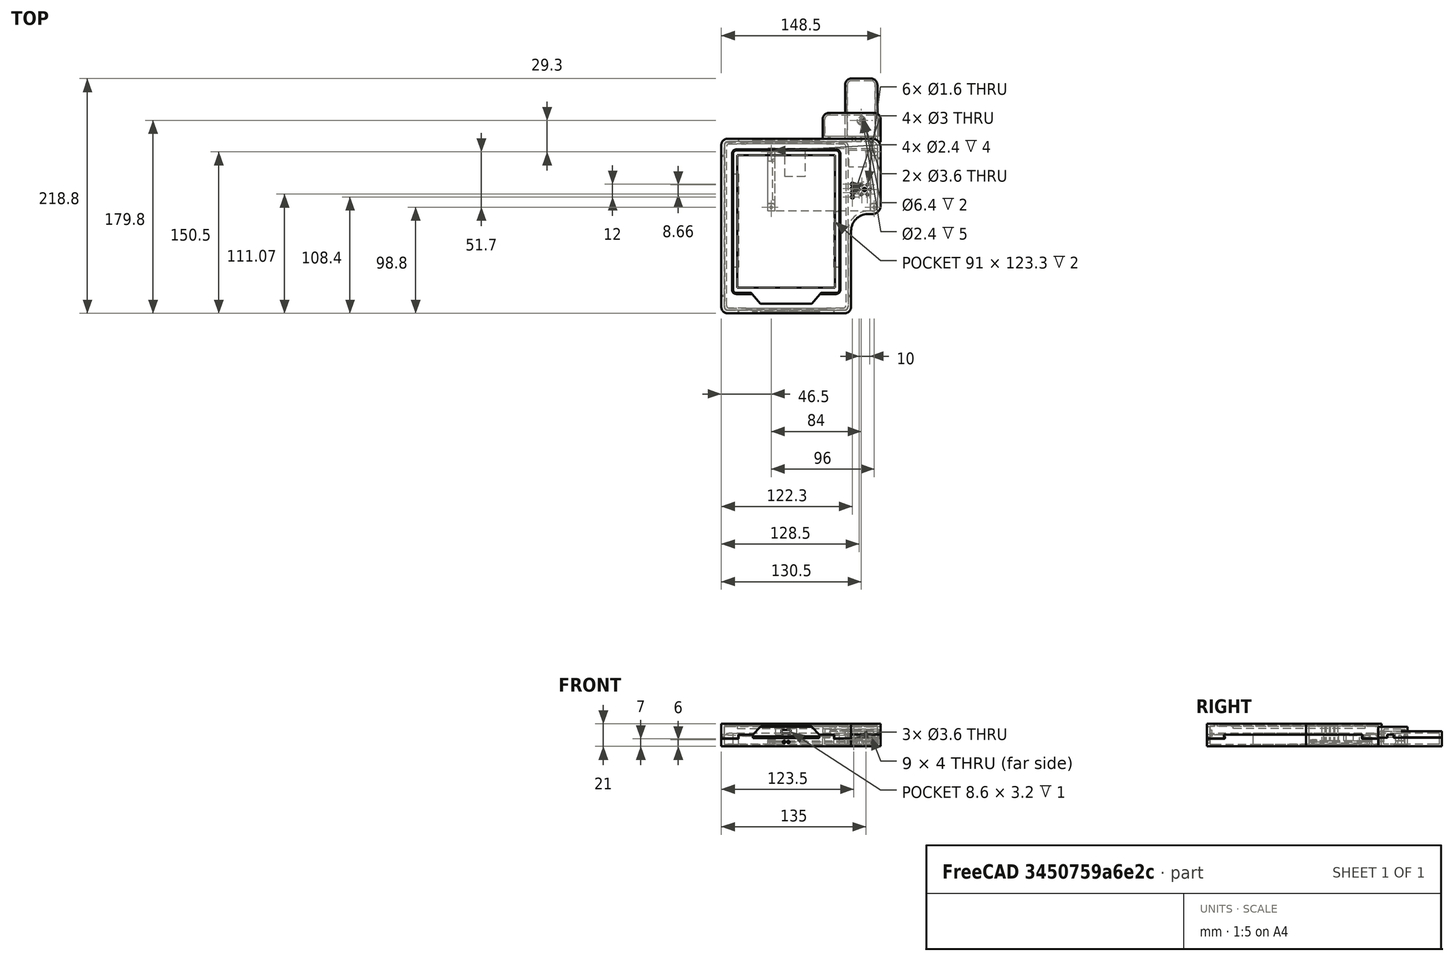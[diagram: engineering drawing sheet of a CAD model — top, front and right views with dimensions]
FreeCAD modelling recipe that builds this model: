
FCSTD DOCUMENT  (FreeCAD 0.18R16131 (Git))
Label: Kobo
License: All rights reserved
LicenseURL: http://en.wikipedia.org/wiki/All_rights_reserved
objects: Sketcher::SketchObject×69, PartDesign::Pocket×30, PartDesign::Pad×20, PartDesign::Plane×18, PartDesign::ShapeBinder×14, PartDesign::Body×10, PartDesign::Fillet×5, PartDesign::SubtractiveLoft×4, PartDesign::AdditiveLoft×4, PartDesign::Chamfer×4, Mesh::Feature×2
note: 236 computed .brp shape members not serialized (recipe doc carries the construction recipe); baked Part::Feature solids carry a one-line shape summary decoded from their .brp

FEATURE [Sketcher::SketchObject] Sketch  label="Kobo-Outline"
  MapMode = 5
  Support = -> [XY_Plane]
  sketch-geometry (4):
    g0: LineSegment StartX=-57.5 StartY=78.4 StartZ=0 EndX=57.5 EndY=78.4 EndZ=0
    g1: LineSegment StartX=57.5 StartY=78.4 StartZ=0 EndX=57.5 EndY=-78.4 EndZ=0
    g2: LineSegment StartX=57.5 StartY=-78.4 StartZ=0 EndX=-57.5 EndY=-78.4 EndZ=0
    g3: LineSegment StartX=-57.5 StartY=-78.4 StartZ=0 EndX=-57.5 EndY=78.4 EndZ=0
  constraints (12):
    c: Coincident(g0,g1)
    c: Coincident(g1,g2)
    c: Coincident(g2,g3)
    c: Coincident(g3,g0)
    c: Horizontal(g0)
    c: Horizontal(g2)
    c: Vertical(g1)
    c: Vertical(g3)
    c: Symmetric(g0,g0,g-2)
    c: Symmetric(g0,g1,g-1)
    c: DistanceY(g1,g1) = 156.8
    c: DistanceX(g2,g2) = 115
FEATURE [Sketcher::SketchObject] Sketch001  label="Vario-Outline"
  MapMode = 5
  Support = -> [XY_Plane]
  sketch-geometry (17):
    g0: LineSegment StartX=-17 StartY=72.5 StartZ=0 EndX=85 EndY=72.5 EndZ=0
    g1: LineSegment StartX=85 StartY=72.5 StartZ=0 EndX=85 EndY=14 EndZ=0
    g2: LineSegment StartX=85 StartY=14 StartZ=0 EndX=-17 EndY=14 EndZ=0
    g3: LineSegment StartX=-17 StartY=14 StartZ=0 EndX=-17 EndY=72.5 EndZ=0
    g4: LineSegment StartX=58.5 StartY=70.9 StartZ=0 EndX=74.5 EndY=70.9 EndZ=0
    g5: LineSegment StartX=74.5 StartY=70.9 StartZ=0 EndX=74.5 EndY=54.9 EndZ=0
    g6: LineSegment StartX=74.5 StartY=54.9 StartZ=0 EndX=58.5 EndY=54.9 EndZ=0
    g7: LineSegment StartX=58.5 StartY=54.9 StartZ=0 EndX=58.5 EndY=70.9 EndZ=0
    g8: Circle CenterX=61.8 CenterY=39 CenterZ=0 NormalX=0 NormalY=0 NormalZ=1 AngleXU=0 Radius=1.5
    g9: Circle CenterX=61.8 CenterY=35 CenterZ=0 NormalX=0 NormalY=0 NormalZ=1 AngleXU=0 Radius=1.5
    g10: Circle CenterX=61.8 CenterY=31 CenterZ=0 NormalX=0 NormalY=0 NormalZ=1 AngleXU=0 Radius=1.5
    g11: Circle CenterX=61.8 CenterY=27 CenterZ=0 NormalX=0 NormalY=0 NormalZ=1 AngleXU=0 Radius=1.5
    g12: Circle CenterX=73 CenterY=34 CenterZ=0 NormalX=0 NormalY=0 NormalZ=1 AngleXU=0 Radius=7
    g13: LineSegment StartX=-1.22 StartY=70 StartZ=0 EndX=17.58 EndY=70 EndZ=0
    g14: LineSegment StartX=17.58 StartY=70 StartZ=0 EndX=17.58 EndY=46 EndZ=0
    g15: LineSegment StartX=17.58 StartY=46 StartZ=0 EndX=-1.22 EndY=46 EndZ=0
    g16: LineSegment StartX=-1.22 StartY=46 StartZ=0 EndX=-1.22 EndY=70 EndZ=0
  constraints (51):
    c: Coincident(g0,g1)
    c: Coincident(g1,g2)
    c: Coincident(g2,g3)
    c: Coincident(g3,g0)
    c: Horizontal(g0)
    c: Horizontal(g2)
    c: Vertical(g1)
    c: Vertical(g3)
    c: DistanceY(g1,g1) = 58.5
    c: DistanceX(g2,g2) = 102
    c: DistanceX(g2,g-1) = 17
    c: DistanceY(g-1,g2) = 14
    c: Coincident(g4,g5)
    c: Coincident(g5,g6)
    c: Coincident(g6,g7)
    c: Coincident(g7,g4)
    c: Horizontal(g4)
    c: Horizontal(g6)
    c: Vertical(g5)
    c: Vertical(g7)
    c: Coincident(g13,g14)
    c: Coincident(g14,g15)
    c: Coincident(g15,g16)
    c: Coincident(g16,g13)
    c: Horizontal(g13)
    c: Horizontal(g15)
    c: Vertical(g14)
    c: Vertical(g16)
    c: Equal(g4,g5)
    c: DistanceX(g4,g4) = 16
    c: Vertical(g8,g9)
    c: Vertical(g9,g10)
    c: Vertical(g10,g11)
    c: Equal(g11,g10)
    c: Equal(g10,g9)
    c: Equal(g9,g8)
    c: Radius(g8) = 1.5
    c: DistanceX(g2,g6) = 75.5
    c: DistanceX(g2,g11) = 78.8
    c: DistanceX(g2,g12) = 90
    c: DistanceY(g2,g11) = 13
    c: DistanceY(g2,g10) = 17
    c: DistanceY(g2,g9) = 21
    c: DistanceY(g2,g8) = 25
    c: DistanceY(g14,g14) = 24
    c: DistanceX(g13,g13) = 18.8
    c: DistanceX(g2,g15) = 15.78
    c: DistanceY(g2,g15) = 32
    c: DistanceY(g1,g5) = 40.9
    c: Radius(g12) = 7
    c: DistanceY(g1,g12) = 20
FEATURE [PartDesign::ShapeBinder] ShapeBinder  label="ShapeBinder-Kobo"
  Support = -> [Sketch]
  TraceSupport = false
FEATURE [PartDesign::ShapeBinder] ShapeBinder001  label="ShapeBinder-Vario"
  Support = -> [Sketch001]
  TraceSupport = false
FEATURE [PartDesign::ShapeBinder] ShapeBinder002
  Support = -> [Sketch]
  TraceSupport = false
FEATURE [Sketcher::SketchObject] Sketch003
  MapMode = 5
  Placement = pos=(0,0,0) rot=(1,0,0;1.5708rad)
  Support = -> [XZ_Plane003]
  sketch-geometry (6):
    g0: LineSegment StartX=-57.4 StartY=6.4 StartZ=0 EndX=57.4 EndY=6.4 EndZ=0
    g1: LineSegment StartX=57.4 StartY=6.4 StartZ=0 EndX=57.4 EndY=-1.1 EndZ=0
    g2: LineSegment StartX=37.4 StartY=-2.6 StartZ=0 EndX=-37.4 EndY=-2.6 EndZ=0
    g3: LineSegment StartX=-57.4 StartY=-1.1 StartZ=0 EndX=-57.4 EndY=6.4 EndZ=0
    g4: LineSegment StartX=-57.4 StartY=-1.1 StartZ=0 EndX=-37.4 EndY=-2.6 EndZ=0
    g5: LineSegment StartX=37.4 StartY=-2.6 StartZ=0 EndX=57.4 EndY=-1.1 EndZ=0
  constraints (16):
    c: Coincident(g0,g1)
    c: Coincident(g3,g0)
    c: Vertical(g1)
    c: Vertical(g3)
    c: Coincident(g2,g5)
    c: Coincident(g1,g5)
    c: Coincident(g2,g4)
    c: Coincident(g3,g4)
    c: Symmetric(g0,g0,g-2)
    c: Equal(g3,g1)
    c: Symmetric(g2,g2,g-2)
    c: DistanceX(g0,g0) = 114.8
    c: DistanceY(g2,g-1) = 2.6
    c: DistanceY(g3,g3) = 7.5
    c: DistanceX(g3,g2) = 20
    c: DistanceY(g2,g0) = 9
FEATURE [PartDesign::Pad] Pad
  Length = 78.2
  Length2 = 78.2
  Placement = pos=(0,0,0) rot=(1,0,0;1.5708rad)
  Profile = -> Sketch003
  Type = 4
FEATURE [Sketcher::SketchObject] Sketch004
  ExternalGeometry = -> [ShapeBinder002]
  MapMode = 5
  Placement = pos=(0,4.2e-15,6.4) rot=(0,0,1;3.14159rad)
  Support = -> [Pad]
  sketch-geometry (4):
    g0: LineSegment StartX=-45.5 StartY=57.4 StartZ=0 EndX=45.5 EndY=57.4 EndZ=0
    g1: LineSegment StartX=45.5 StartY=57.4 StartZ=0 EndX=45.5 EndY=-65.9 EndZ=0
    g2: LineSegment StartX=45.5 StartY=-65.9 StartZ=0 EndX=-45.5 EndY=-65.9 EndZ=0
    g3: LineSegment StartX=-45.5 StartY=-65.9 StartZ=0 EndX=-45.5 EndY=57.4 EndZ=0
  constraints (11):
    c: Coincident(g0,g1)
    c: Coincident(g1,g2)
    c: Coincident(g2,g3)
    c: Coincident(g3,g0)
    c: Vertical(g1)
    c: Vertical(g3)
    c: Symmetric(g0,g0,g-2)
    c: DistanceX(g-3,g0) = 12
    c: DistanceY(g0,g-3) = 21
    c: Horizontal(g2)
    c: DistanceY(g-4,g1) = 12.5
FEATURE [PartDesign::Pocket] Pocket
  BaseFeature = -> Pad
  Length = 2
  Length2 = 100
  Placement = pos=(0,0,0) rot=(1,0,0;1.5708rad)
  Profile = -> Sketch004
  Type = 0
FEATURE [Sketcher::SketchObject] Sketch005
  ExternalGeometry = -> [ShapeBinder002]
  MapMode = 5
  Placement = pos=(0,-1.7e-15,-2.6) rot=(1,0,0;3.14159rad)
  Support = -> [Pocket]
  sketch-geometry (8):
    g0: LineSegment StartX=-53.5 StartY=76.4 StartZ=0 EndX=53.5 EndY=76.4 EndZ=0
    g1: LineSegment StartX=55.5 StartY=74.4 StartZ=0 EndX=55.5 EndY=-74.4 EndZ=0
    g2: LineSegment StartX=53.5 StartY=-76.4 StartZ=0 EndX=-53.5 EndY=-76.4 EndZ=0
    g3: LineSegment StartX=-55.5 StartY=-74.4 StartZ=0 EndX=-55.5 EndY=74.4 EndZ=0
    g4: ArcOfCircle CenterX=-53.5 CenterY=74.4 CenterZ=0 NormalX=0 NormalY=0 NormalZ=1 AngleXU=0 Radius=2 StartAngle=1.5708 EndAngle=3.14159
    g5: ArcOfCircle CenterX=53.5 CenterY=74.4 CenterZ=0 NormalX=0 NormalY=0 NormalZ=1 AngleXU=0 Radius=2 StartAngle=-9e-16 EndAngle=1.5708
    g6: ArcOfCircle CenterX=53.5 CenterY=-74.4 CenterZ=0 NormalX=0 NormalY=0 NormalZ=1 AngleXU=0 Radius=2 StartAngle=4.71239 EndAngle=6.28319
    g7: ArcOfCircle CenterX=-53.5 CenterY=-74.4 CenterZ=0 NormalX=0 NormalY=0 NormalZ=1 AngleXU=0 Radius=2 StartAngle=3.14159 EndAngle=4.71239
  constraints (20):
    c: Horizontal(g0)
    c: Horizontal(g2)
    c: Vertical(g1)
    c: Vertical(g3)
    c: Tangent(g0,g4) = 1.5708
    c: Tangent(g3,g4) = 1.5708
    c: Tangent(g0,g5) = 1.5708
    c: Tangent(g1,g5) = 1.5708
    c: Tangent(g1,g6) = 1.5708
    c: Tangent(g2,g6) = 1.5708
    c: Tangent(g2,g7) = 1.5708
    c: Tangent(g3,g7) = 1.5708
    c: Vertical(g4,g7)
    c: Vertical(g5,g6)
    c: Horizontal(g4,g5)
    c: DistanceX(g3,g4) = 2
    c: DistanceX(g-3,g4) = 4
    c: DistanceY(g4,g-3) = 4
    c: DistanceX(g6,g-4) = 4
    c: DistanceY(g-4,g6) = 4
FEATURE [PartDesign::Pocket] Pocket001
  BaseFeature = -> Pocket
  Length = 2.6
  Length2 = 100
  Placement = pos=(0,0,0) rot=(1,0,0;1.5708rad)
  Profile = -> Sketch005
  Type = 0
FEATURE [PartDesign::Fillet] Fillet
  Base = -> Pocket001 [Edge24,Edge21,Edge4,Edge3]
  BaseFeature = -> Pocket001
  Placement = pos=(0,0,0) rot=(1,0,0;1.5708rad)
  Radius = 3
FEATURE [PartDesign::ShapeBinder] ShapeBinder003
  Support = -> [Sketch001]
  TraceSupport = false
FEATURE [Sketcher::SketchObject] Sketch006
  ExternalGeometry = -> [ShapeBinder003]
  MapMode = 5
  Support = -> [XY_Plane004]
  sketch-geometry (12):
    g0: LineSegment StartX=-10.625 StartY=72.5 StartZ=0 EndX=78.625 EndY=72.5 EndZ=0
    g1: LineSegment StartX=85 StartY=65.575 StartZ=0 EndX=85 EndY=20.925 EndZ=0
    g2: LineSegment StartX=78.625 StartY=14 StartZ=0 EndX=-10.625 EndY=14 EndZ=0
    g3: LineSegment StartX=-17 StartY=20.925 StartZ=0 EndX=-17 EndY=65.575 EndZ=0
    g4: LineSegment StartX=78.625 StartY=20.925 StartZ=0 EndX=85 EndY=20.925 EndZ=0
    g5: LineSegment StartX=78.625 StartY=14 StartZ=0 EndX=78.625 EndY=20.925 EndZ=0
    g6: LineSegment StartX=85 StartY=65.575 StartZ=0 EndX=78.625 EndY=65.575 EndZ=0
    g7: LineSegment StartX=78.625 StartY=65.575 StartZ=0 EndX=78.625 EndY=72.5 EndZ=0
    g8: LineSegment StartX=-10.625 StartY=72.5 StartZ=0 EndX=-10.625 EndY=65.575 EndZ=0
    g9: LineSegment StartX=-10.625 StartY=65.575 StartZ=0 EndX=-17 EndY=65.575 EndZ=0
    g10: LineSegment StartX=-17 StartY=20.925 StartZ=0 EndX=-10.625 EndY=20.925 EndZ=0
    g11: LineSegment StartX=-10.625 StartY=20.925 StartZ=0 EndX=-10.625 EndY=14 EndZ=0
  constraints (36):
    c: Horizontal(g0)
    c: Horizontal(g2)
    c: Vertical(g1)
    c: Vertical(g3)
    c: Coincident(g5,g4)
    c: Horizontal(g4)
    c: Vertical(g5)
    c: Coincident(g6,g7)
    c: Horizontal(g6)
    c: Vertical(g7)
    c: Coincident(g8,g9)
    c: Horizontal(g9)
    c: Vertical(g8)
    c: Coincident(g10,g11)
    c: Horizontal(g10)
    c: Vertical(g11)
    c: Coincident(g0,g8)
    c: Coincident(g3,g9)
    c: Coincident(g0,g7)
    c: Coincident(g1,g6)
    c: Coincident(g1,g4)
    c: Coincident(g2,g5)
    c: Coincident(g2,g11)
    c: Coincident(g3,g10)
    c: Vertical(g8,g10)
    c: Vertical(g6,g4)
    c: Horizontal(g6,g8)
    c: Horizontal(g10,g4)
    c: Vertical(g3,g-3)
    c: Vertical(g-4,g1)
    c: Horizontal(g2,g-5)
    c: Horizontal(g-4,g0)
    c: Equal(g8,g11)
    c: Equal(g10,g4)
    c: DistanceY(g3,g3) = 44.65
    c: DistanceX(g0,g0) = 89.25
FEATURE [PartDesign::Pad] Pad001  label="PCB"
  Length = 1.2
  Length2 = 100
  Profile = -> Sketch006
  Type = 0
FEATURE [Sketcher::SketchObject] Sketch007
  ExternalGeometry = -> [ShapeBinder003]
  MapMode = 5
  Placement = pos=(0,0,1.2) rot=(0,0,1;0rad)
  Support = -> [Pad001]
  sketch-geometry (4):
    g0: LineSegment StartX=58.5 StartY=70.9 StartZ=0 EndX=74.5 EndY=70.9 EndZ=0
    g1: LineSegment StartX=74.5 StartY=70.9 StartZ=0 EndX=74.5 EndY=54.9 EndZ=0
    g2: LineSegment StartX=74.5 StartY=54.9 StartZ=0 EndX=58.5 EndY=54.9 EndZ=0
    g3: LineSegment StartX=58.5 StartY=54.9 StartZ=0 EndX=58.5 EndY=70.9 EndZ=0
  constraints (10):
    c: Coincident(g0,g1)
    c: Coincident(g1,g2)
    c: Coincident(g2,g3)
    c: Coincident(g3,g0)
    c: Horizontal(g0)
    c: Horizontal(g2)
    c: Vertical(g1)
    c: Vertical(g3)
    c: Coincident(g-4,g2)
    c: Coincident(g-3,g0)
FEATURE [PartDesign::Pad] Pad002  label="GPS"
  BaseFeature = -> Pad001
  Length = 6.5
  Length2 = 100
  Profile = -> Sketch007
  Type = 0
FEATURE [Sketcher::SketchObject] Sketch008
  ExternalGeometry = -> [ShapeBinder003]
  MapMode = 5
  Placement = pos=(0,0,1.2) rot=(0,0,1;0rad)
  Support = -> [Pad002]
  sketch-geometry (4):
    g0: Circle CenterX=61.8 CenterY=39 CenterZ=0 NormalX=0 NormalY=0 NormalZ=1 AngleXU=0 Radius=1.5
    g1: Circle CenterX=61.8 CenterY=35 CenterZ=0 NormalX=0 NormalY=0 NormalZ=1 AngleXU=0 Radius=1.5
    g2: Circle CenterX=61.8 CenterY=31 CenterZ=0 NormalX=0 NormalY=0 NormalZ=1 AngleXU=0 Radius=1.5
    g3: Circle CenterX=61.8 CenterY=27 CenterZ=0 NormalX=0 NormalY=0 NormalZ=1 AngleXU=0 Radius=1.5
  constraints (8):
    c: Equal(g3,g2)
    c: Equal(g2,g1)
    c: Equal(g1,g0)
    c: Radius(g0) = 1.5
    c: Coincident(g3,g-6)
    c: Coincident(g-5,g2)
    c: Coincident(g-4,g1)
    c: Coincident(g-3,g0)
FEATURE [PartDesign::Pad] Pad003  label="LED"
  BaseFeature = -> Pad002
  Length = 15
  Length2 = 100
  Profile = -> Sketch008
  Type = 0
FEATURE [Sketcher::SketchObject] Sketch009
  ExternalGeometry = -> [ShapeBinder003]
  MapMode = 5
  Placement = pos=(0,0,1.2) rot=(0,0,1;0rad)
  Support = -> [Pad003]
  sketch-geometry (1):
    g0: Circle CenterX=73 CenterY=34 CenterZ=0 NormalX=0 NormalY=0 NormalZ=1 AngleXU=0 Radius=7
  constraints (2):
    c: Radius(g0) = 7
    c: Coincident(g0,g-3)
FEATURE [PartDesign::Pad] Pad004  label="PIEZO"
  BaseFeature = -> Pad003
  Length = 5
  Length2 = 100
  Profile = -> Sketch009
  Type = 0
FEATURE [Sketcher::SketchObject] Sketch010
  ExternalGeometry = -> [ShapeBinder003]
  MapMode = 5
  Placement = pos=(0,0,1.2) rot=(0,0,1;0rad)
  Support = -> [Pad004]
  sketch-geometry (4):
    g0: LineSegment StartX=-1.22 StartY=70 StartZ=0 EndX=17.58 EndY=70 EndZ=0
    g1: LineSegment StartX=17.58 StartY=70 StartZ=0 EndX=17.58 EndY=46 EndZ=0
    g2: LineSegment StartX=17.58 StartY=46 StartZ=0 EndX=-1.22 EndY=46 EndZ=0
    g3: LineSegment StartX=-1.22 StartY=46 StartZ=0 EndX=-1.22 EndY=70 EndZ=0
  constraints (10):
    c: Coincident(g0,g1)
    c: Coincident(g1,g2)
    c: Coincident(g2,g3)
    c: Coincident(g3,g0)
    c: Horizontal(g0)
    c: Horizontal(g2)
    c: Vertical(g1)
    c: Vertical(g3)
    c: Coincident(g0,g-3)
    c: Coincident(g-4,g2)
FEATURE [PartDesign::Pad] Pad005  label="IMU"
  BaseFeature = -> Pad004
  Length = 4.8
  Length2 = 100
  Profile = -> Sketch010
  Type = 0
FEATURE [PartDesign::Body] Body004  label="Vario"
  Group = -> [ShapeBinder003,Sketch006,Pad001,Sketch007,Pad002,Sketch008,Pad003,Sketch009,Pad004,Sketch010,Pad005]
  Origin = -> Origin004
  Placement = pos=(0,0,4) rot=(0,0,1;0rad)
  Tip = -> Pad005
FEATURE [Sketcher::SketchObject] Sketch012
  ExternalGeometry = -> [Fillet]
  MapMode = 5
  Placement = pos=(0,-78.2,3.46e-14) rot=(1,0,0;1.5708rad)
  Support = -> [Fillet]
  sketch-geometry (4):
    g0: LineSegment StartX=-4.3 StartY=3.2 StartZ=0 EndX=4.3 EndY=3.2 EndZ=0
    g1: LineSegment StartX=4.3 StartY=3.2 StartZ=0 EndX=4.3 EndY=9e-16 EndZ=0
    g2: LineSegment StartX=4.3 StartY=9e-16 StartZ=0 EndX=-4.3 EndY=9e-16 EndZ=0
    g3: LineSegment StartX=-4.3 StartY=9e-16 StartZ=0 EndX=-4.3 EndY=3.2 EndZ=0
  constraints (11):
    c: Coincident(g0,g1)
    c: Coincident(g1,g2)
    c: Coincident(g2,g3)
    c: Coincident(g3,g0)
    c: Horizontal(g0)
    c: Vertical(g1)
    c: Vertical(g3)
    c: Symmetric(g2,g1,g-2)
    c: DistanceX(g2,g2) = 8.6
    c: DistanceY(g1,g1) = 3.2
    c: DistanceY(g-3,g1) = 2.6
FEATURE [PartDesign::Pocket] Pocket003
  BaseFeature = -> Fillet
  Length = 1
  Length2 = 100
  Placement = pos=(0,0,0) rot=(1,0,0;1.5708rad)
  Profile = -> Sketch012
  Type = 0
FEATURE [Sketcher::SketchObject] Sketch013
  ExternalGeometry = -> [Pocket003]
  MapMode = 5
  Placement = pos=(0,78.2,-3.46e-14) rot=(-1,0,0;1.5708rad)
  Support = -> [Pocket003]
  sketch-geometry (4):
    g0: LineSegment StartX=-10 StartY=1 StartZ=0 EndX=10 EndY=1 EndZ=0
    g1: LineSegment StartX=10 StartY=1 StartZ=0 EndX=10 EndY=-4.6 EndZ=0
    g2: LineSegment StartX=10 StartY=-4.6 StartZ=0 EndX=-10 EndY=-4.6 EndZ=0
    g3: LineSegment StartX=-10 StartY=-4.6 StartZ=0 EndX=-10 EndY=1 EndZ=0
  constraints (11):
    c: Coincident(g0,g1)
    c: Coincident(g1,g2)
    c: Coincident(g2,g3)
    c: Coincident(g3,g0)
    c: Horizontal(g0)
    c: Vertical(g1)
    c: Vertical(g3)
    c: Symmetric(g2,g1,g-2)
    c: DistanceX(g2,g2) = 20
    c: DistanceY(g1,g1) = 5.6
    c: DistanceY(g0,g-3) = 1.6
FEATURE [PartDesign::Pocket] Pocket004
  BaseFeature = -> Pocket003
  Length = 1
  Length2 = 100
  Placement = pos=(0,0,0) rot=(1,0,0;1.5708rad)
  Profile = -> Sketch013
  Type = 0
FEATURE [PartDesign::Body] Body003  label="Kobo"
  Group = -> [ShapeBinder002,Sketch003,Pad,Sketch004,Pocket,Sketch005,Pocket001,Fillet,Sketch012,Pocket003,Sketch013,Pocket004]
  Origin = -> Origin003
  Placement = pos=(0,0,12) rot=(0,0,1;0rad)
  Tip = -> Pocket004
FEATURE [PartDesign::ShapeBinder] ShapeBinder004  label="ShapeBinder-Kobo-Cover"
  Support = -> [Sketch]
  TraceSupport = false
FEATURE [PartDesign::ShapeBinder] ShapeBinder005  label="ShapeBinder-Vario-Cover"
  Support = -> [Sketch001]
  TraceSupport = false
FEATURE [Sketcher::SketchObject] Sketch014
  ExternalGeometry = -> [ShapeBinder004,ShapeBinder005]
  MapMode = 5
  Support = -> [XY_Plane002]
  sketch-geometry (12):
    g0: LineSegment StartX=-54.5 StartY=81.4 StartZ=0 EndX=80 EndY=81.4 EndZ=0
    g1: LineSegment StartX=88 StartY=73.4 StartZ=0 EndX=88 EndY=19 EndZ=0
    g2: LineSegment StartX=54.5 StartY=-81.4 StartZ=0 EndX=-54.5 EndY=-81.4 EndZ=0
    g3: LineSegment StartX=-60.5 StartY=-75.4 StartZ=0 EndX=-60.5 EndY=75.4 EndZ=0
    g4: LineSegment StartX=76 StartY=11 StartZ=0 EndX=80 EndY=11 EndZ=0
    g5: LineSegment StartX=60.5 StartY=-75.4 StartZ=0 EndX=60.5 EndY=-4.5 EndZ=0
    g6: ArcOfCircle CenterX=-54.5 CenterY=75.4 CenterZ=0 NormalX=0 NormalY=0 NormalZ=1 AngleXU=0 Radius=6 StartAngle=1.5708 EndAngle=3.14159
    g7: ArcOfCircle CenterX=80 CenterY=73.4 CenterZ=0 NormalX=0 NormalY=0 NormalZ=1 AngleXU=0 Radius=8 StartAngle=-9e-16 EndAngle=1.5708
    g8: ArcOfCircle CenterX=80 CenterY=19 CenterZ=0 NormalX=0 NormalY=0 NormalZ=1 AngleXU=0 Radius=8 StartAngle=4.71239 EndAngle=6.28319
    g9: ArcOfCircle CenterX=76 CenterY=-4.5 CenterZ=0 NormalX=0 NormalY=0 NormalZ=1 AngleXU=0 Radius=15.5 StartAngle=1.5708 EndAngle=3.14159
    g10: ArcOfCircle CenterX=54.5 CenterY=-75.4 CenterZ=0 NormalX=0 NormalY=0 NormalZ=1 AngleXU=0 Radius=6 StartAngle=4.71239 EndAngle=6.28319
    g11: ArcOfCircle CenterX=-54.5 CenterY=-75.4 CenterZ=0 NormalX=0 NormalY=0 NormalZ=1 AngleXU=0 Radius=6 StartAngle=3.14159 EndAngle=4.71239
  constraints (30):
    c: Horizontal(g0)
    c: Horizontal(g2)
    c: Vertical(g1)
    c: Vertical(g3)
    c: Horizontal(g4)
    c: Vertical(g5)
    c: Tangent(g0,g6) = 1.5708
    c: Tangent(g3,g6) = 1.5708
    c: Tangent(g0,g7) = 1.5708
    c: Tangent(g1,g7) = 1.5708
    c: Tangent(g1,g8) = 1.5708
    c: Tangent(g4,g8) = -1.5708
    c: Tangent(g4,g9) = 1.5708
    c: Tangent(g5,g9) = 1.5708
    c: Tangent(g2,g10) = 1.5708
    c: Tangent(g5,g10) = -1.5708
    c: Tangent(g2,g11) = 1.5708
    c: Tangent(g3,g11) = 1.5708
    c: Vertical(g6,g11)
    c: Horizontal(g11,g10)
    c: DistanceX(g3,g11) = 6
    c: DistanceY(g-3,g0) = 3
    c: DistanceX(g3,g-3) = 3
    c: DistanceX(g-5,g1) = 3
    c: DistanceY(g4,g-5) = 3
    c: DistanceY(g2,g-4) = 3
    c: DistanceX(g-4,g5) = 3
    c: DistanceX(g4,g4) = 4
    c: Vertical(g8,g7)
    c: DistanceX(g7,g1) = 8
FEATURE [PartDesign::Pad] Pad007
  Length = 10
  Length2 = 100
  Profile = -> Sketch014
  Reversed = true
  Type = 0
FEATURE [Sketcher::SketchObject] Sketch015
  ExternalGeometry = -> [ShapeBinder,ShapeBinder001]
  MapMode = 5
  Support = -> [XY_Plane001]
  sketch-geometry (12):
    g0: LineSegment StartX=-54.5 StartY=81.4 StartZ=0 EndX=80 EndY=81.4 EndZ=0
    g1: LineSegment StartX=88 StartY=73.4 StartZ=0 EndX=88 EndY=19 EndZ=0
    g2: LineSegment StartX=54.5 StartY=-81.4 StartZ=0 EndX=-54.5 EndY=-81.4 EndZ=0
    g3: LineSegment StartX=-60.5 StartY=-75.4 StartZ=0 EndX=-60.5 EndY=75.4 EndZ=0
    g4: LineSegment StartX=76 StartY=11 StartZ=0 EndX=80 EndY=11 EndZ=0
    g5: LineSegment StartX=60.5 StartY=-75.4 StartZ=0 EndX=60.5 EndY=-4.5 EndZ=0
    g6: ArcOfCircle CenterX=-54.5 CenterY=75.4 CenterZ=0 NormalX=0 NormalY=0 NormalZ=1 AngleXU=0 Radius=6 StartAngle=1.5708 EndAngle=3.14159
    g7: ArcOfCircle CenterX=80 CenterY=73.4 CenterZ=0 NormalX=0 NormalY=0 NormalZ=1 AngleXU=0 Radius=8 StartAngle=0 EndAngle=1.5708
    g8: ArcOfCircle CenterX=80 CenterY=19 CenterZ=0 NormalX=0 NormalY=0 NormalZ=1 AngleXU=0 Radius=8 StartAngle=4.71239 EndAngle=6.28319
    g9: ArcOfCircle CenterX=76 CenterY=-4.5 CenterZ=0 NormalX=0 NormalY=0 NormalZ=1 AngleXU=0 Radius=15.5 StartAngle=1.5708 EndAngle=3.14159
    g10: ArcOfCircle CenterX=54.5 CenterY=-75.4 CenterZ=0 NormalX=0 NormalY=0 NormalZ=1 AngleXU=0 Radius=6 StartAngle=4.71239 EndAngle=6.28319
    g11: ArcOfCircle CenterX=-54.5 CenterY=-75.4 CenterZ=0 NormalX=0 NormalY=0 NormalZ=1 AngleXU=0 Radius=6 StartAngle=3.14159 EndAngle=4.71239
  constraints (30):
    c: Horizontal(g0)
    c: Horizontal(g2)
    c: Vertical(g1)
    c: Vertical(g3)
    c: Horizontal(g4)
    c: Vertical(g5)
    c: Tangent(g0,g6) = 1.5708
    c: Tangent(g3,g6) = 1.5708
    c: Tangent(g0,g7) = 1.5708
    c: Tangent(g1,g7) = 1.5708
    c: Tangent(g1,g8) = 1.5708
    c: Tangent(g4,g8) = -1.5708
    c: Tangent(g4,g9) = 1.5708
    c: Tangent(g5,g9) = 1.5708
    c: Tangent(g2,g10) = 1.5708
    c: Tangent(g5,g10) = -1.5708
    c: Tangent(g2,g11) = 1.5708
    c: Tangent(g3,g11) = 1.5708
    c: Vertical(g11,g6)
    c: Horizontal(g11,g10)
    c: Vertical(g8,g7)
    c: DistanceY(g2,g11) = 6
    c: DistanceX(g-4,g5) = 3
    c: DistanceX(g3,g-4) = 3
    c: DistanceY(g-3,g0) = 3
    c: DistanceY(g7,g0) = 8
    c: DistanceX(g-5,g1) = 3
    c: DistanceY(g4,g-5) = 3
    c: DistanceX(g4,g4) = 4
    c: DistanceY(g2,g-4) = 3
FEATURE [PartDesign::Pad] Pad008
  Length = 11
  Length2 = 100
  Profile = -> Sketch015
  Type = 0
FEATURE [Sketcher::SketchObject] Sketch016
  ExternalGeometry = -> [ShapeBinder,ShapeBinder001]
  MapMode = 5
  Placement = pos=(0,0,11) rot=(0,0,1;0rad)
  Support = -> [Pad008]
  sketch-geometry (12):
    g0: LineSegment StartX=-54.7 StartY=78.6 StartZ=0 EndX=80.2 EndY=78.6 EndZ=0
    g1: LineSegment StartX=85.2 StartY=73.6 StartZ=0 EndX=85.2 EndY=18.8 EndZ=0
    g2: LineSegment StartX=54.7 StartY=-78.6 StartZ=0 EndX=-54.7 EndY=-78.6 EndZ=0
    g3: LineSegment StartX=-57.7 StartY=-75.6 StartZ=0 EndX=-57.7 EndY=75.6 EndZ=0
    g4: LineSegment StartX=76.2 StartY=13.8 StartZ=0 EndX=80.2 EndY=13.8 EndZ=0
    g5: LineSegment StartX=57.7 StartY=-75.6 StartZ=0 EndX=57.7 EndY=-4.7 EndZ=0
    g6: ArcOfCircle CenterX=-54.7 CenterY=75.6 CenterZ=0 NormalX=0 NormalY=0 NormalZ=1 AngleXU=0 Radius=3 StartAngle=1.5708 EndAngle=3.14159
    g7: ArcOfCircle CenterX=80.2 CenterY=73.6 CenterZ=0 NormalX=0 NormalY=0 NormalZ=1 AngleXU=0 Radius=5 StartAngle=1.3e-15 EndAngle=1.5708
    g8: ArcOfCircle CenterX=80.2 CenterY=18.8 CenterZ=0 NormalX=0 NormalY=0 NormalZ=1 AngleXU=0 Radius=5 StartAngle=4.71239 EndAngle=6.28319
    g9: ArcOfCircle CenterX=76.2 CenterY=-4.7 CenterZ=0 NormalX=0 NormalY=0 NormalZ=1 AngleXU=0 Radius=18.5 StartAngle=1.5708 EndAngle=3.14159
    g10: ArcOfCircle CenterX=54.7 CenterY=-75.6 CenterZ=0 NormalX=0 NormalY=0 NormalZ=1 AngleXU=0 Radius=3 StartAngle=4.71239 EndAngle=6.28319
    g11: ArcOfCircle CenterX=-54.7 CenterY=-75.6 CenterZ=0 NormalX=0 NormalY=0 NormalZ=1 AngleXU=0 Radius=3 StartAngle=3.14159 EndAngle=4.71239
  constraints (30):
    c: Horizontal(g0)
    c: Horizontal(g2)
    c: Vertical(g1)
    c: Vertical(g3)
    c: Horizontal(g4)
    c: Vertical(g5)
    c: Tangent(g0,g6) = 1.5708
    c: Tangent(g3,g6) = 1.5708
    c: Tangent(g0,g7) = 1.5708
    c: Tangent(g1,g7) = 1.5708
    c: Tangent(g1,g8) = 1.5708
    c: Tangent(g4,g8) = -1.5708
    c: Tangent(g4,g9) = 1.5708
    c: Tangent(g5,g9) = 1.5708
    c: Tangent(g2,g10) = 1.5708
    c: Tangent(g5,g10) = -1.5708
    c: Tangent(g2,g11) = 1.5708
    c: Tangent(g3,g11) = 1.5708
    c: Vertical(g6,g11)
    c: Horizontal(g11,g10)
    c: Vertical(g7,g8)
    c: DistanceY(g2,g11) = 3
    c: DistanceX(g3,g-5) = 0.2
    c: DistanceY(g2,g-5) = 0.2
    c: DistanceX(g-5,g5) = 0.2
    c: DistanceY(g4,g-4) = 0.2
    c: DistanceX(g-4,g1) = 0.2
    c: DistanceY(g-3,g0) = 0.2
    c: DistanceY(g7,g0) = 5
    c: DistanceX(g4,g4) = 4
FEATURE [PartDesign::Pocket] Pocket005
  BaseFeature = -> Pad008
  Length = 9
  Length2 = 100
  Profile = -> Sketch016
  Type = 0
FEATURE [Sketcher::SketchObject] Sketch017
  ExternalGeometry = -> [ShapeBinder004,ShapeBinder005]
  MapMode = 5
  Placement = pos=(0,0,-10) rot=(1,0,0;3.14159rad)
  Support = -> [Pad007]
  sketch-geometry (12):
    g0: LineSegment StartX=-54.7 StartY=78.6 StartZ=0 EndX=54.7 EndY=78.6 EndZ=0
    g1: LineSegment StartX=85.2 StartY=-18.8 StartZ=0 EndX=85.2 EndY=-73.6 EndZ=0
    g2: LineSegment StartX=80.2 StartY=-78.6 StartZ=0 EndX=-54.7 EndY=-78.6 EndZ=0
    g3: LineSegment StartX=-57.7 StartY=-75.6 StartZ=0 EndX=-57.7 EndY=75.6 EndZ=0
    g4: LineSegment StartX=80.2 StartY=-13.8 StartZ=0 EndX=76.2 EndY=-13.8 EndZ=0
    g5: LineSegment StartX=57.7 StartY=4.7 StartZ=0 EndX=57.7 EndY=75.6 EndZ=0
    g6: ArcOfCircle CenterX=-54.7 CenterY=75.6 CenterZ=0 NormalX=0 NormalY=0 NormalZ=1 AngleXU=0 Radius=3 StartAngle=1.5708 EndAngle=3.14159
    g7: ArcOfCircle CenterX=54.7 CenterY=75.6 CenterZ=0 NormalX=0 NormalY=0 NormalZ=1 AngleXU=0 Radius=3 StartAngle=6e-16 EndAngle=1.5708
    g8: ArcOfCircle CenterX=-54.7 CenterY=-75.6 CenterZ=0 NormalX=0 NormalY=0 NormalZ=1 AngleXU=0 Radius=3 StartAngle=3.14159 EndAngle=4.71239
    g9: ArcOfCircle CenterX=80.2 CenterY=-73.6 CenterZ=0 NormalX=0 NormalY=0 NormalZ=1 AngleXU=0 Radius=5 StartAngle=4.71239 EndAngle=6.28319
    g10: ArcOfCircle CenterX=80.2 CenterY=-18.8 CenterZ=0 NormalX=0 NormalY=0 NormalZ=1 AngleXU=0 Radius=5 StartAngle=2e-16 EndAngle=1.5708
    g11: ArcOfCircle CenterX=76.2 CenterY=4.7 CenterZ=0 NormalX=0 NormalY=0 NormalZ=1 AngleXU=0 Radius=18.5 StartAngle=3.14159 EndAngle=4.71239
  constraints (30):
    c: Horizontal(g0)
    c: Horizontal(g2)
    c: Vertical(g1)
    c: Vertical(g3)
    c: Horizontal(g4)
    c: Vertical(g5)
    c: Tangent(g0,g6) = 1.5708
    c: Tangent(g3,g6) = 1.5708
    c: Tangent(g0,g7) = 1.5708
    c: Tangent(g5,g7) = -1.5708
    c: Tangent(g2,g8) = 1.5708
    c: Tangent(g3,g8) = 1.5708
    c: Tangent(g1,g9) = 1.5708
    c: Tangent(g2,g9) = 1.5708
    c: Tangent(g1,g10) = 1.5708
    c: Tangent(g4,g10) = -1.5708
    c: Tangent(g4,g11) = 1.5708
    c: Tangent(g5,g11) = 1.5708
    c: Vertical(g9,g10)
    c: Vertical(g6,g8)
    c: Horizontal(g6,g7)
    c: DistanceY(g2,g8) = 3
    c: DistanceY(g2,g-4) = 0.2
    c: DistanceX(g3,g-4) = 0.2
    c: DistanceY(g-3,g0) = 0.2
    c: DistanceX(g-3,g5) = 0.2
    c: DistanceX(g-5,g1) = 0.2
    c: DistanceY(g2,g9) = 5
    c: DistanceX(g4,g4) = 4
    c: DistanceY(g-5,g4) = 0.2
FEATURE [PartDesign::Pocket] Pocket006
  BaseFeature = -> Pad007
  Length = 8
  Length2 = 100
  Profile = -> Sketch017
  Type = 0
FEATURE [Sketcher::SketchObject] Sketch018
  ExternalGeometry = -> [ShapeBinder004]
  MapMode = 5
  Support = -> [Pocket006]
  sketch-geometry (12):
    g0: LineSegment StartX=-46.5 StartY=70.4 StartZ=0 EndX=46.5 EndY=70.4 EndZ=0
    g1: LineSegment StartX=49.5 StartY=67.4 StartZ=0 EndX=49.5 EndY=-59.4 EndZ=0
    g2: LineSegment StartX=46.5 StartY=-62.4 StartZ=0 EndX=32.5 EndY=-62.4 EndZ=0
    g3: LineSegment StartX=-49.5 StartY=-59.4 StartZ=0 EndX=-49.5 EndY=67.4 EndZ=0
    g4: ArcOfCircle CenterX=-46.5 CenterY=67.4 CenterZ=0 NormalX=0 NormalY=0 NormalZ=1 AngleXU=0 Radius=3 StartAngle=1.5708 EndAngle=3.14159
    g5: ArcOfCircle CenterX=46.5 CenterY=67.4 CenterZ=0 NormalX=0 NormalY=0 NormalZ=1 AngleXU=0 Radius=3 StartAngle=1.9e-15 EndAngle=1.5708
    g6: ArcOfCircle CenterX=46.5 CenterY=-59.4 CenterZ=0 NormalX=0 NormalY=0 NormalZ=1 AngleXU=0 Radius=3 StartAngle=4.71239 EndAngle=6.28319
    g7: ArcOfCircle CenterX=-46.5 CenterY=-59.4 CenterZ=0 NormalX=0 NormalY=0 NormalZ=1 AngleXU=0 Radius=3 StartAngle=3.14159 EndAngle=4.71239
    g8: LineSegment StartX=32.5 StartY=-62.4 StartZ=0 EndX=24 EndY=-72.4 EndZ=0
    g9: LineSegment StartX=24 StartY=-72.4 StartZ=0 EndX=-24 EndY=-72.4 EndZ=0
    g10: LineSegment StartX=-24 StartY=-72.4 StartZ=0 EndX=-32.5 EndY=-62.4 EndZ=0
    g11: LineSegment StartX=-32.5 StartY=-62.4 StartZ=0 EndX=-46.5 EndY=-62.4 EndZ=0
  constraints (31):
    c: Horizontal(g0)
    c: Horizontal(g2)
    c: Vertical(g1)
    c: Vertical(g3)
    c: Tangent(g0,g4) = 1.5708
    c: Tangent(g3,g4) = 1.5708
    c: Tangent(g0,g5) = 1.5708
    c: Tangent(g1,g5) = 1.5708
    c: Tangent(g1,g6) = 1.5708
    c: Tangent(g2,g6) = 1.5708
    c: Coincident(g11,g7) = 1.5708
    c: Tangent(g3,g7) = 1.5708
    c: Vertical(g4,g7)
    c: Vertical(g5,g6)
    c: Horizontal(g4,g5)
    c: DistanceY(g4,g0) = 3
    c: Coincident(g8,g9)
    c: Coincident(g9,g10)
    c: Coincident(g2,g8)
    c: Tangent(g2,g11)
    c: Coincident(g10,g11)
    c: DistanceX(g-4,g3) = 8
    c: DistanceY(g0,g-3) = 8
    c: DistanceY(g-4,g8) = 6
    c: DistanceY(g-4,g2) = 16
    c: Symmetric(g9,g8,g-2)
    c: Equal(g11,g2)
    c: DistanceX(g9,g9) = 48
    c: DistanceX(g11,g11) = 14
    c: DistanceX(g1,g-4) = 8
    c: Vertical(g7,g7)
FEATURE [PartDesign::Pocket] Pocket007
  BaseFeature = -> Pocket006
  Length = 2
  Length2 = 100
  Profile = -> Sketch018
  Type = 0
FEATURE [Sketcher::SketchObject] Sketch019
  ExternalGeometry = -> [ShapeBinder001]
  MapMode = 5
  Placement = pos=(0,0,2) rot=(0,0,1;0rad)
  Support = -> [Pocket005]
  sketch-geometry (8):
    g0: LineSegment StartX=-17 StartY=72.5 StartZ=0 EndX=-10.75 EndY=72.5 EndZ=0
    g1: LineSegment StartX=-10.75 StartY=72.5 StartZ=0 EndX=-10.75 EndY=14 EndZ=0
    g2: LineSegment StartX=-10.75 StartY=14 StartZ=0 EndX=-17 EndY=14 EndZ=0
    g3: LineSegment StartX=-17 StartY=14 StartZ=0 EndX=-17 EndY=72.5 EndZ=0
    g4: LineSegment StartX=78.75 StartY=72.5 StartZ=0 EndX=85 EndY=72.5 EndZ=0
    g5: LineSegment StartX=85 StartY=72.5 StartZ=0 EndX=85 EndY=14 EndZ=0
    g6: LineSegment StartX=85 StartY=14 StartZ=0 EndX=78.75 EndY=14 EndZ=0
    g7: LineSegment StartX=78.75 StartY=14 StartZ=0 EndX=78.75 EndY=72.5 EndZ=0
  constraints (20):
    c: Coincident(g0,g1)
    c: Coincident(g1,g2)
    c: Coincident(g2,g3)
    c: Coincident(g3,g0)
    c: Horizontal(g0)
    c: Horizontal(g2)
    c: Vertical(g1)
    c: Coincident(g4,g5)
    c: Coincident(g5,g6)
    c: Coincident(g6,g7)
    c: Coincident(g7,g4)
    c: Horizontal(g4)
    c: Horizontal(g6)
    c: Vertical(g7)
    c: Coincident(g2,g-4)
    c: Coincident(g0,g-3)
    c: Coincident(g4,g-3)
    c: Coincident(g5,g-4)
    c: Equal(g0,g4)
    c: DistanceX(g0,g4) = 89.5
FEATURE [PartDesign::Pad] Pad009
  BaseFeature = -> Pocket005
  Length = 4
  Length2 = 100
  Profile = -> Sketch019
  Type = 0
FEATURE [Sketcher::SketchObject] Sketch020
  ExternalGeometry = -> [ShapeBinder001]
  MapMode = 5
  Placement = pos=(0,0,6) rot=(0,0,1;0rad)
  Support = -> [Pad009]
  sketch-geometry (8):
    g0: LineSegment StartX=-17 StartY=65.7 StartZ=0 EndX=-10.75 EndY=65.7 EndZ=0
    g1: LineSegment StartX=-10.75 StartY=65.7 StartZ=0 EndX=-10.75 EndY=20.8 EndZ=0
    g2: LineSegment StartX=-10.75 StartY=20.8 StartZ=0 EndX=-17 EndY=20.8 EndZ=0
    g3: LineSegment StartX=-17 StartY=20.8 StartZ=0 EndX=-17 EndY=65.7 EndZ=0
    g4: LineSegment StartX=78.75 StartY=65.7 StartZ=0 EndX=85 EndY=65.7 EndZ=0
    g5: LineSegment StartX=85 StartY=65.7 StartZ=0 EndX=85 EndY=20.8 EndZ=0
    g6: LineSegment StartX=85 StartY=20.8 StartZ=0 EndX=78.75 EndY=20.8 EndZ=0
    g7: LineSegment StartX=78.75 StartY=20.8 StartZ=0 EndX=78.75 EndY=65.7 EndZ=0
  constraints (24):
    c: Coincident(g0,g1)
    c: Coincident(g1,g2)
    c: Coincident(g2,g3)
    c: Coincident(g3,g0)
    c: Horizontal(g0)
    c: Horizontal(g2)
    c: Vertical(g1)
    c: Vertical(g3)
    c: Coincident(g4,g5)
    c: Coincident(g5,g6)
    c: Coincident(g6,g7)
    c: Coincident(g7,g4)
    c: Horizontal(g4)
    c: Horizontal(g6)
    c: Vertical(g5)
    c: Vertical(g7)
    c: PointOnObject(g2,g-5)
    c: PointOnObject(g5,g-6)
    c: Horizontal(g0,g4)
    c: Horizontal(g1,g6)
    c: Equal(g0,g4)
    c: DistanceY(g0,g-5) = 6.8
    c: DistanceY(g-5,g2) = 6.8
    c: DistanceX(g0,g4) = 89.5
FEATURE [PartDesign::Pocket] Pocket008
  BaseFeature = -> Pad009
  Length = 2
  Length2 = 100
  Profile = -> Sketch020
  Type = 0
FEATURE [Sketcher::SketchObject] Sketch021
  ExternalGeometry = -> [ShapeBinder001,ShapeBinder]
  MapMode = 5
  Placement = pos=(0,0,2) rot=(0,0,1;0rad)
  Support = -> [Pocket008]
  sketch-geometry (8):
    g0: LineSegment StartX=-49.5 StartY=48.4 StartZ=0 EndX=-44.5 EndY=48.4 EndZ=0
    g1: LineSegment StartX=-44.5 StartY=48.4 StartZ=0 EndX=-44.5 EndY=-38.4 EndZ=0
    g2: LineSegment StartX=-44.5 StartY=-38.4 StartZ=0 EndX=-49.5 EndY=-38.4 EndZ=0
    g3: LineSegment StartX=-49.5 StartY=-38.4 StartZ=0 EndX=-49.5 EndY=48.4 EndZ=0
    g4: LineSegment StartX=44.5 StartY=13.6 StartZ=0 EndX=49.5 EndY=13.6 EndZ=0
    g5: LineSegment StartX=49.5 StartY=13.6 StartZ=0 EndX=49.5 EndY=-38.4 EndZ=0
    g6: LineSegment StartX=49.5 StartY=-38.4 StartZ=0 EndX=44.5 EndY=-38.4 EndZ=0
    g7: LineSegment StartX=44.5 StartY=-38.4 StartZ=0 EndX=44.5 EndY=13.6 EndZ=0
  constraints (24):
    c: Coincident(g0,g1)
    c: Coincident(g1,g2)
    c: Coincident(g2,g3)
    c: Coincident(g3,g0)
    c: Horizontal(g0)
    c: Horizontal(g2)
    c: Vertical(g1)
    c: Vertical(g3)
    c: Coincident(g4,g5)
    c: Coincident(g5,g6)
    c: Coincident(g6,g7)
    c: Coincident(g7,g4)
    c: Horizontal(g4)
    c: Horizontal(g6)
    c: Vertical(g5)
    c: Vertical(g7)
    c: DistanceX(g0,g0) = 5
    c: DistanceX(g6,g6) = 5
    c: DistanceX(g5,g-4) = 8
    c: DistanceX(g-4,g2) = 8
    c: DistanceY(g-4,g2) = 40
    c: DistanceY(g0,g-5) = 30
    c: DistanceY(g4,g-3) = 0.4
    c: Horizontal(g6,g1)
FEATURE [PartDesign::Pad] Pad010
  BaseFeature = -> Pocket008
  Length = 10
  Length2 = 100
  Profile = -> Sketch021
  Type = 0
FEATURE [Sketcher::SketchObject] Sketch022
  ExternalGeometry = -> [ShapeBinder005]
  MapMode = 5
  Support = -> [Pocket007]
  sketch-geometry (18):
    g0: Circle CenterX=61.8 CenterY=39 CenterZ=0 NormalX=0 NormalY=0 NormalZ=1 AngleXU=0 Radius=1.5
    g1: Circle CenterX=61.8 CenterY=35 CenterZ=0 NormalX=0 NormalY=0 NormalZ=1 AngleXU=0 Radius=1.5
    g2: Circle CenterX=61.8 CenterY=31 CenterZ=0 NormalX=0 NormalY=0 NormalZ=1 AngleXU=0 Radius=1.5
    g3: Circle CenterX=61.8 CenterY=27 CenterZ=0 NormalX=0 NormalY=0 NormalZ=1 AngleXU=0 Radius=1.5
    g4: Circle CenterX=73 CenterY=34 CenterZ=0 NormalX=0 NormalY=0 NormalZ=1 AngleXU=0 Radius=1.6
    g5: Circle CenterX=70.5 CenterY=38.3301 CenterZ=0 NormalX=0 NormalY=0 NormalZ=1 AngleXU=0 Radius=0.8
    g6: Circle CenterX=75.5 CenterY=38.3301 CenterZ=0 NormalX=0 NormalY=0 NormalZ=1 AngleXU=0 Radius=0.8
    g7: Circle CenterX=78 CenterY=34 CenterZ=0 NormalX=0 NormalY=0 NormalZ=1 AngleXU=0 Radius=0.8
    g8: Circle CenterX=75.5 CenterY=29.6699 CenterZ=0 NormalX=0 NormalY=0 NormalZ=1 AngleXU=0 Radius=0.8
    g9: Circle CenterX=70.5 CenterY=29.6699 CenterZ=0 NormalX=0 NormalY=0 NormalZ=1 AngleXU=0 Radius=0.8
    g10: Circle CenterX=68 CenterY=34 CenterZ=0 NormalX=0 NormalY=0 NormalZ=1 AngleXU=0 Radius=0.8
    g11: LineSegment [constr] StartX=75.5 StartY=29.6699 StartZ=0 EndX=78 EndY=34 EndZ=0
    g12: LineSegment [constr] StartX=78 StartY=34 StartZ=0 EndX=75.5 EndY=38.3301 EndZ=0
    g13: LineSegment [constr] StartX=75.5 StartY=38.3301 StartZ=0 EndX=70.5 EndY=38.3301 EndZ=0
    g14: LineSegment [constr] StartX=70.5 StartY=38.3301 StartZ=0 EndX=68 EndY=34 EndZ=0
    g15: LineSegment [constr] StartX=68 StartY=34 StartZ=0 EndX=70.5 EndY=29.6699 EndZ=0
    g16: LineSegment [constr] StartX=70.5 StartY=29.6699 StartZ=0 EndX=75.5 EndY=29.6699 EndZ=0
    g17: Circle [constr] CenterX=73 CenterY=34 CenterZ=0 NormalX=0 NormalY=0 NormalZ=1 AngleXU=0 Radius=5
  constraints (38):
    c: Coincident(g0,g-3)
    c: Coincident(g1,g-4)
    c: Coincident(g2,g-5)
    c: Coincident(g3,g-6)
    c: Coincident(g4,g-7)
    c: Equal(g0,g1)
    c: Equal(g1,g2)
    c: Equal(g2,g3)
    c: Radius(g0) = 1.5
    c: Radius(g4) = 1.6
    c: Coincident(g11,g12)
    c: Coincident(g12,g13)
    c: Coincident(g13,g14)
    c: Coincident(g14,g15)
    c: Coincident(g15,g16)
    c: Coincident(g16,g11)
    c: Equal(g11, g12-g16) x5
    c: PointOnObject(g11,g17)
    c: PointOnObject(g12,g17)
    c: PointOnObject(g13,g17)
    c: PointOnObject(g14,g17)
    c: PointOnObject(g15,g17)
    c: PointOnObject(g16,g17)
    c: Coincident(g4,g17)
    c: Coincident(g5,g13)
    c: Coincident(g6,g12)
    c: Coincident(g7,g11)
    c: Coincident(g8,g11)
    c: Coincident(g9,g15)
    c: Coincident(g10,g14)
    c: Horizontal(g4,g7)
    c: DistanceX(g4,g7) = 5
    c: Equal(g9,g10)
    c: Equal(g10,g5)
    c: Equal(g5,g6)
    c: Equal(g6,g7)
    c: Equal(g7,g8)
    c: Radius(g6) = 0.8
FEATURE [PartDesign::Pocket] Pocket009
  BaseFeature = -> Pocket007
  Length = 2
  Length2 = 100
  Profile = -> Sketch022
  Type = 0
FEATURE [Sketcher::SketchObject] Sketch023
  MapMode = 5
  Placement = pos=(0,81.4,0) rot=(0,0.707107,0.707107;3.14159rad)
  Support = -> [Pocket009]
  sketch-geometry (4):
    g0: LineSegment StartX=-24 StartY=-3 StartZ=0 EndX=24 EndY=-3 EndZ=0
    g1: LineSegment StartX=24 StartY=-3 StartZ=0 EndX=31 EndY=-10 EndZ=0
    g2: LineSegment StartX=31 StartY=-10 StartZ=0 EndX=-31 EndY=-10 EndZ=0
    g3: LineSegment StartX=-31 StartY=-10 StartZ=0 EndX=-24 EndY=-3 EndZ=0
  constraints (10):
    c: Coincident(g0,g1)
    c: Coincident(g1,g2)
    c: Coincident(g2,g3)
    c: Coincident(g3,g0)
    c: Symmetric(g0,g0,g-2)
    c: Symmetric(g1,g2,g-2)
    c: DistanceY(g0,g-1) = 3
    c: DistanceX(g0,g0) = 48
    c: DistanceX(g2,g2) = 62
    c: DistanceY(g1,g0) = 7
FEATURE [PartDesign::Pocket] Pocket010
  BaseFeature = -> Pocket009
  Length = 5
  Length2 = 100
  Profile = -> Sketch023
  Type = 1
FEATURE [Sketcher::SketchObject] Sketch024
  MapMode = 5
  Placement = pos=(0,-81.4,0) rot=(1,0,0;1.5708rad)
  Support = -> [Pad010]
  sketch-geometry (4):
    g0: LineSegment StartX=-31 StartY=11 StartZ=0 EndX=31 EndY=11 EndZ=0
    g1: LineSegment StartX=31 StartY=11 StartZ=0 EndX=31 EndY=9 EndZ=0
    g2: LineSegment StartX=31 StartY=9 StartZ=0 EndX=-31 EndY=9 EndZ=0
    g3: LineSegment StartX=-31 StartY=9 StartZ=0 EndX=-31 EndY=11 EndZ=0
  constraints (11):
    c: Coincident(g0,g1)
    c: Coincident(g1,g2)
    c: Coincident(g2,g3)
    c: Coincident(g3,g0)
    c: Horizontal(g2)
    c: Vertical(g1)
    c: Vertical(g3)
    c: DistanceX(g0,g0) = 62
    c: Symmetric(g0,g0,g-2)
    c: DistanceY(g3,g3) = 2
    c: DistanceY(g-1,g2) = 9
FEATURE [PartDesign::Pocket] Pocket011
  BaseFeature = -> Pad010
  Length = 5
  Length2 = 100
  Profile = -> Sketch024
  Type = 1
FEATURE [Sketcher::SketchObject] Sketch025
  ExternalGeometry = -> [ShapeBinder,ShapeBinder001]
  MapMode = 5
  Placement = pos=(0,0,11) rot=(0,0,1;0rad)
  Support = -> [Pocket011]
  sketch-geometry (32):
    g0: LineSegment StartX=-54.5 StartY=81.4 StartZ=0 EndX=-44.5 EndY=81.4 EndZ=0
    g1: LineSegment StartX=-44.5 StartY=81.4 StartZ=0 EndX=-44.5 EndY=78.6 EndZ=0
    g2: LineSegment StartX=-57.7 StartY=65.4 StartZ=0 EndX=-60.5 EndY=65.4 EndZ=0
    g3: LineSegment StartX=-60.5 StartY=65.4 StartZ=0 EndX=-60.5 EndY=75.4 EndZ=0
    g4: LineSegment StartX=-54.7 StartY=78.6 StartZ=0 EndX=-44.5 EndY=78.6 EndZ=0
    g5: LineSegment StartX=-57.7 StartY=65.4 StartZ=0 EndX=-57.7 EndY=75.6 EndZ=0
    g6: LineSegment StartX=70 StartY=81.4 StartZ=0 EndX=80 EndY=81.4 EndZ=0
    g7: LineSegment StartX=88 StartY=73.4 StartZ=0 EndX=88 EndY=63.4 EndZ=0
    g8: LineSegment StartX=88 StartY=63.4 StartZ=0 EndX=85.2 EndY=63.4 EndZ=0
    g9: LineSegment StartX=70 StartY=78.6 StartZ=0 EndX=70 EndY=81.4 EndZ=0
    g10: LineSegment StartX=70 StartY=78.6 StartZ=0 EndX=80 EndY=78.6 EndZ=0
    g11: LineSegment StartX=85.2 StartY=73.4 StartZ=0 EndX=85.2 EndY=63.4 EndZ=0
    g12: LineSegment StartX=-60.5 StartY=-65.4 StartZ=0 EndX=-57.7 EndY=-65.4 EndZ=0
    g13: LineSegment StartX=-44.5 StartY=-78.6 StartZ=0 EndX=-44.5 EndY=-81.4 EndZ=0
    g14: LineSegment StartX=-44.5 StartY=-81.4 StartZ=0 EndX=-54.5 EndY=-81.4 EndZ=0
    g15: LineSegment StartX=-60.5 StartY=-75.4 StartZ=0 EndX=-60.5 EndY=-65.4 EndZ=0
    g16: LineSegment StartX=-44.5 StartY=-78.6 StartZ=0 EndX=-54.7 EndY=-78.6 EndZ=0
    g17: LineSegment StartX=-57.7 StartY=-75.6 StartZ=0 EndX=-57.7 EndY=-65.4 EndZ=0
    g18: LineSegment StartX=57.7 StartY=-65.4 StartZ=0 EndX=60.5 EndY=-65.4 EndZ=0
    g19: LineSegment StartX=60.5 StartY=-65.4 StartZ=0 EndX=60.5 EndY=-75.4 EndZ=0
    g20: LineSegment StartX=54.5 StartY=-81.4 StartZ=0 EndX=44.5 EndY=-81.4 EndZ=0
    g21: LineSegment StartX=44.5 StartY=-81.4 StartZ=0 EndX=44.5 EndY=-78.6 EndZ=0
    g22: LineSegment StartX=57.7 StartY=-65.4 StartZ=0 EndX=57.7 EndY=-75.6 EndZ=0
    g23: LineSegment StartX=54.7 StartY=-78.6 StartZ=0 EndX=44.5 EndY=-78.6 EndZ=0
    g24: ArcOfCircle CenterX=-54.5 CenterY=75.4 CenterZ=0 NormalX=0 NormalY=0 NormalZ=1 AngleXU=0 Radius=6 StartAngle=1.5708 EndAngle=3.14159
    g25: ArcOfCircle CenterX=-54.7 CenterY=75.6 CenterZ=0 NormalX=0 NormalY=0 NormalZ=1 AngleXU=0 Radius=3 StartAngle=1.5708 EndAngle=3.14159
    g26: ArcOfCircle CenterX=80 CenterY=73.4 CenterZ=0 NormalX=0 NormalY=0 NormalZ=1 AngleXU=0 Radius=5.2 StartAngle=-1.092e-13 EndAngle=1.5708
    g27: ArcOfCircle CenterX=80 CenterY=73.4 CenterZ=0 NormalX=0 NormalY=0 NormalZ=1 AngleXU=0 Radius=8 StartAngle=0 EndAngle=1.5708
    g28: ArcOfCircle CenterX=54.7 CenterY=-75.6 CenterZ=0 NormalX=0 NormalY=0 NormalZ=1 AngleXU=0 Radius=3 StartAngle=4.71239 EndAngle=6.28319
    g29: ArcOfCircle CenterX=54.5 CenterY=-75.4 CenterZ=0 NormalX=0 NormalY=0 NormalZ=1 AngleXU=0 Radius=6 StartAngle=4.71239 EndAngle=6.28319
    g30: ArcOfCircle CenterX=-54.5 CenterY=-75.4 CenterZ=0 NormalX=0 NormalY=0 NormalZ=1 AngleXU=0 Radius=6 StartAngle=3.14159 EndAngle=4.71239
    g31: ArcOfCircle CenterX=-54.7 CenterY=-75.6 CenterZ=0 NormalX=0 NormalY=0 NormalZ=1 AngleXU=0 Radius=3 StartAngle=3.14159 EndAngle=4.71239
  constraints (89):
    c: Coincident(g0,g1)
    c: Coincident(g2,g3)
    c: Horizontal(g0)
    c: Horizontal(g2)
    c: Vertical(g1)
    c: Vertical(g3)
    c: Horizontal(g4)
    c: Vertical(g5)
    c: Coincident(g7,g8)
    c: Coincident(g9,g6)
    c: Horizontal(g6)
    c: Horizontal(g8)
    c: Vertical(g7)
    c: Vertical(g9)
    c: Horizontal(g10)
    c: Vertical(g11)
    c: Coincident(g13,g14)
    c: Coincident(g15,g12)
    c: Horizontal(g12)
    c: Horizontal(g14)
    c: Vertical(g13)
    c: Vertical(g15)
    c: Horizontal(g16)
    c: Vertical(g17)
    c: Coincident(g18,g19)
    c: Coincident(g20,g21)
    c: Horizontal(g18)
    c: Horizontal(g20)
    c: Vertical(g19)
    c: Vertical(g21)
    c: Horizontal(g23)
    c: Vertical(g22)
    c: Coincident(g4,g1)
    c: Coincident(g5,g2)
    c: Coincident(g9,g10)
    c: Coincident(g11,g8)
    c: Coincident(g18,g22)
    c: Coincident(g23,g21)
    c: Coincident(g12,g17)
    c: Coincident(g16,g13)
    c: Tangent(g0,g24) = 1.5708
    c: Tangent(g3,g24) = 1.5708
    c: Tangent(g4,g25) = 1.5708
    c: Tangent(g5,g25) = 1.5708
    c: Tangent(g10,g26) = 1.5708
    c: Tangent(g11,g26) = 1.5708
    c: Tangent(g6,g27) = 1.5708
    c: Tangent(g7,g27) = 1.5708
    c: Tangent(g22,g28) = 1.5708
    c: Tangent(g23,g28) = 1.5708
    c: Tangent(g19,g29) = 1.5708
    c: Tangent(g20,g29) = 1.5708
    c: Tangent(g14,g30) = 1.5708
    c: Tangent(g15,g30) = 1.5708
    c: Tangent(g16,g31) = 1.5708
    c: Tangent(g17,g31) = 1.5708
    c: Vertical(g24,g30)
    c: Horizontal(g30,g29)
    c: Horizontal(g31,g28)
    c: Vertical(g31,g25)
    c: DistanceX(g3,g24) = 6
    c: DistanceY(g25,g4) = 3
    c: DistanceX(g3,g-3) = 3
    c: DistanceY(g-3,g0) = 3
    c: DistanceX(g5,g-3) = 0.2
    c: DistanceY(g-3,g4) = 0.2
    c: Equal(g3,g0)
    c: DistanceX(g0,g0) = 10
    c: DistanceY(g14,g-5) = 3
    c: DistanceX(g15,g-5) = 3
    c: DistanceY(g16,g-5) = 0.2
    c: DistanceX(g17,g-5) = 0.2
    c: Equal(g14,g15)
    c: Equal(g0,g14)
    c: DistanceY(g20,g-5) = 3
    c: DistanceX(g-5,g19) = 3
    c: DistanceY(g23,g-5) = 0.2
    c: DistanceX(g-5,g22) = 0.2
    c: Equal(g19,g20)
    c: Equal(g20,g14)
    c: DistanceX(g6,g7) = 8
    c: DistanceX(g-4) = 85
    c: DistanceX(g-4,g7) = 3
    c: DistanceX(g-4,g11) = 0.2
    c: DistanceY(g-3,g6) = 3
    c: DistanceY(g-3,g10) = 0.2
    c: Horizontal(g11,g7)
    c: Equal(g7,g6)
    c: Equal(g7,g19)
FEATURE [PartDesign::Pocket] Pocket012
  BaseFeature = -> Pocket011
  Length = 4
  Length2 = 100
  Profile = -> Sketch025
  Type = 0
FEATURE [Sketcher::SketchObject] Sketch026
  ExternalGeometry = -> [ShapeBinder004,ShapeBinder005,Pocket010]
  MapMode = 5
  Placement = pos=(0,0,-10) rot=(1,0,0;3.14159rad)
  Support = -> [Pocket010]
  sketch-geometry (32):
    g0: LineSegment StartX=-54.5 StartY=81.4 StartZ=0 EndX=-44.7 EndY=81.4 EndZ=0
    g1: LineSegment StartX=-57.7 StartY=65.6 StartZ=0 EndX=-60.5 EndY=65.6 EndZ=0
    g2: LineSegment StartX=-60.5 StartY=65.6 StartZ=0 EndX=-60.5 EndY=75.4 EndZ=0
    g3: LineSegment StartX=-54.7 StartY=78.6 StartZ=0 EndX=-44.7 EndY=78.6 EndZ=0
    g4: LineSegment StartX=-57.7 StartY=65.6 StartZ=0 EndX=-57.7 EndY=75.6 EndZ=0
    g5: LineSegment StartX=54.5 StartY=81.4 StartZ=0 EndX=44.7 EndY=81.4 EndZ=0
    g6: LineSegment StartX=44.7 StartY=81.4 StartZ=0 EndX=44.7 EndY=78.6 EndZ=0
    g7: LineSegment StartX=57.7 StartY=65.6 StartZ=0 EndX=60.5 EndY=65.6 EndZ=0
    g8: LineSegment StartX=60.5 StartY=65.6 StartZ=0 EndX=60.5 EndY=75.4 EndZ=0
    g9: LineSegment StartX=54.7 StartY=78.6 StartZ=0 EndX=44.7 EndY=78.6 EndZ=0
    g10: LineSegment StartX=57.7 StartY=65.6 StartZ=0 EndX=57.7 EndY=75.6 EndZ=0
    g11: LineSegment StartX=-54.5 StartY=-81.4 StartZ=0 EndX=-44.7 EndY=-81.4 EndZ=0
    g12: LineSegment StartX=-44.7 StartY=-81.4 StartZ=0 EndX=-44.7 EndY=-78.6 EndZ=0
    g13: LineSegment StartX=-57.7 StartY=-65.6 StartZ=0 EndX=-60.5 EndY=-65.6 EndZ=0
    g14: LineSegment StartX=-60.5 StartY=-65.6 StartZ=0 EndX=-60.5 EndY=-75.4 EndZ=0
    g15: LineSegment StartX=-54.7 StartY=-78.6 StartZ=0 EndX=-44.7 EndY=-78.6 EndZ=0
    g16: LineSegment StartX=-57.7 StartY=-65.6 StartZ=0 EndX=-57.7 EndY=-75.6 EndZ=0
    g17: LineSegment StartX=80 StartY=-81.4 StartZ=0 EndX=70.2 EndY=-81.4 EndZ=0
    g18: LineSegment StartX=70.2 StartY=-81.4 StartZ=0 EndX=70.2 EndY=-78.6 EndZ=0
    g19: LineSegment StartX=85.2 StartY=-63.6 StartZ=0 EndX=88 EndY=-63.6 EndZ=0
    g20: LineSegment StartX=88 StartY=-63.6 StartZ=0 EndX=88 EndY=-73.4 EndZ=0
    g21: LineSegment StartX=80.2 StartY=-78.6 StartZ=0 EndX=70.2 EndY=-78.6 EndZ=0
    g22: LineSegment StartX=85.2 StartY=-63.6 StartZ=0 EndX=85.2 EndY=-73.6 EndZ=0
    g23: ArcOfCircle CenterX=-54.7 CenterY=-75.6 CenterZ=0 NormalX=0 NormalY=0 NormalZ=1 AngleXU=0 Radius=3 StartAngle=3.14159 EndAngle=4.71239
    g24: ArcOfCircle CenterX=-54.5 CenterY=-75.4 CenterZ=0 NormalX=0 NormalY=0 NormalZ=1 AngleXU=0 Radius=6 StartAngle=3.14159 EndAngle=4.71239
    g25: ArcOfCircle CenterX=80.2 CenterY=-73.6 CenterZ=0 NormalX=0 NormalY=0 NormalZ=1 AngleXU=0 Radius=5 StartAngle=4.71239 EndAngle=6.28319
    g26: ArcOfCircle CenterX=80 CenterY=-73.4 CenterZ=0 NormalX=0 NormalY=0 NormalZ=1 AngleXU=0 Radius=8 StartAngle=4.71239 EndAngle=6.28319
    g27: ArcOfCircle CenterX=54.7 CenterY=75.6 CenterZ=0 NormalX=0 NormalY=0 NormalZ=1 AngleXU=0 Radius=3 StartAngle=-9e-16 EndAngle=1.5708
    g28: ArcOfCircle CenterX=54.5 CenterY=75.4 CenterZ=0 NormalX=0 NormalY=0 NormalZ=1 AngleXU=0 Radius=6 StartAngle=1.2e-15 EndAngle=1.5708
    g29: ArcOfCircle CenterX=-54.5 CenterY=75.4 CenterZ=0 NormalX=0 NormalY=0 NormalZ=1 AngleXU=0 Radius=6 StartAngle=1.5708 EndAngle=3.14159
    g30: ArcOfCircle CenterX=-54.7 CenterY=75.6 CenterZ=0 NormalX=0 NormalY=0 NormalZ=1 AngleXU=0 Radius=3 StartAngle=1.5708 EndAngle=3.14159
    g31: LineSegment StartX=-44.7 StartY=81.4 StartZ=0 EndX=-44.7 EndY=78.6 EndZ=0
  constraints (88):
    c: Coincident(g1,g2)
    c: Horizontal(g0)
    c: Horizontal(g1)
    c: Vertical(g2)
    c: Horizontal(g3)
    c: Vertical(g4)
    c: Coincident(g5,g6)
    c: Coincident(g7,g8)
    c: Horizontal(g5)
    c: Horizontal(g7)
    c: Vertical(g6)
    c: Vertical(g8)
    c: Horizontal(g9)
    c: Vertical(g10)
    c: Coincident(g11,g12)
    c: Coincident(g13,g14)
    c: Horizontal(g11)
    c: Horizontal(g13)
    c: Vertical(g12)
    c: Vertical(g14)
    c: Horizontal(g15)
    c: Vertical(g16)
    c: Coincident(g17,g18)
    c: Coincident(g19,g20)
    c: Horizontal(g17)
    c: Horizontal(g19)
    c: Vertical(g18)
    c: Vertical(g20)
    c: Horizontal(g21)
    c: Vertical(g22)
    c: Coincident(g18,g21)
    c: Coincident(g22,g19)
    c: Coincident(g15,g12)
    c: Coincident(g13,g16)
    c: Coincident(g6,g9)
    c: Coincident(g10,g7)
    c: Coincident(g1,g4)
    c: Tangent(g15,g23) = -1.5708
    c: Tangent(g16,g23) = -1.5708
    c: Tangent(g11,g24) = -1.5708
    c: Tangent(g14,g24) = -1.5708
    c: Tangent(g21,g25) = 1.5708
    c: Tangent(g22,g25) = 1.5708
    c: Tangent(g17,g26) = 1.5708
    c: Tangent(g20,g26) = 1.5708
    c: Tangent(g9,g27) = -1.5708
    c: Tangent(g10,g27) = -1.5708
    c: Tangent(g5,g28) = -1.5708
    c: Tangent(g8,g28) = -1.5708
    c: Tangent(g0,g29) = 1.5708
    c: Tangent(g2,g29) = 1.5708
    c: Tangent(g3,g30) = 1.5708
    c: Tangent(g4,g30) = 1.5708
    c: Equal(g0,g2)
    c: Equal(g2,g5)
    c: Equal(g5,g8)
    c: Equal(g8,g20)
    c: Equal(g20,g17)
    c: Equal(g17,g11)
    c: Equal(g11,g14)
    c: DistanceX(g2,g0) = 6
    c: DistanceY(g-3,g0) = 3
    c: DistanceX(g2,g-3) = 3
    c: DistanceX(g4,g-3) = 0.2
    c: DistanceY(g-3,g3) = 0.2
    c: DistanceX(g-3,g8) = 3
    c: DistanceX(g-3,g10) = 0.2
    c: DistanceY(g-3,g5) = 3
    c: DistanceY(g-3,g9) = 0.2
    c: DistanceY(g11,g-5) = 3
    c: DistanceY(g15,g-5) = 0.2
    c: DistanceX(g16,g-5) = 0.2
    c: DistanceX(g14,g-5) = 3
    c: DistanceX(g17,g20) = 8
    c: DistanceX(g-4,g20) = 3
    c: DistanceY(g17,g-5) = 3
    c: DistanceX(g-4,g22) = 0.2
    c: DistanceY(g21,g-5) = 0.2
    c: DistanceX(g0,g0) = 9.8
    c: DistanceY(g4,g3) = 3
    c: Vertical(g23,g30)
    c: Vertical(g24,g29)
    c: Coincident(g0,g31)
    c: Coincident(g3,g31)
    c: Vertical(g31)
    c: Horizontal(g27,g30)
    c: Horizontal(g29,g28)
    c: Vertical(g25,g-6)
FEATURE [PartDesign::Pad] Pad011
  BaseFeature = -> Pocket010
  Length = 3.8
  Length2 = 100
  Profile = -> Sketch026
  Type = 0
FEATURE [Sketcher::SketchObject] Sketch027  label="HoleLB"
  ExternalGeometry = -> [Pocket012]
  MapMode = 5
  Placement = pos=(0,-65.4,0) rot=(1,0,0;1.5708rad)
  Support = -> [Pocket012]
  sketch-geometry (4):
    g0: LineSegment StartX=-60.5 StartY=9.4 StartZ=0 EndX=-57.7 EndY=9.4 EndZ=0
    g1: LineSegment StartX=-57.7 StartY=9.4 StartZ=0 EndX=-57.7 EndY=7 EndZ=0
    g2: LineSegment StartX=-57.7 StartY=7 StartZ=0 EndX=-60.5 EndY=7 EndZ=0
    g3: LineSegment StartX=-60.5 StartY=7 StartZ=0 EndX=-60.5 EndY=9.4 EndZ=0
  constraints (11):
    c: Coincident(g0,g1)
    c: Coincident(g1,g2)
    c: Coincident(g2,g3)
    c: Coincident(g3,g0)
    c: Horizontal(g0)
    c: Horizontal(g2)
    c: Vertical(g1)
    c: Vertical(g3)
    c: Coincident(g2,g-3)
    c: PointOnObject(g0,g-4)
    c: DistanceY(g3,g3) = 2.4
FEATURE [Sketcher::SketchObject] Sketch028  label="HoleRT"
  ExternalGeometry = -> [Pocket012]
  MapMode = 5
  Placement = pos=(0,63.4,0) rot=(0,0.707107,0.707107;3.14159rad)
  sketch-geometry (4):
    g0: LineSegment StartX=-88 StartY=9.4 StartZ=0 EndX=-85.2 EndY=9.4 EndZ=0
    g1: LineSegment StartX=-85.2 StartY=9.4 StartZ=0 EndX=-85.2 EndY=7 EndZ=0
    g2: LineSegment StartX=-85.2 StartY=7 StartZ=0 EndX=-88 EndY=7 EndZ=0
    g3: LineSegment StartX=-88 StartY=7 StartZ=0 EndX=-88 EndY=9.4 EndZ=0
  constraints (11):
    c: Coincident(g0,g1)
    c: Coincident(g1,g2)
    c: Coincident(g2,g3)
    c: Coincident(g3,g0)
    c: Horizontal(g0)
    c: Horizontal(g2)
    c: Vertical(g1)
    c: Vertical(g3)
    c: DistanceY(g3,g3) = 2.4
    c: Coincident(g1,g-3)
    c: PointOnObject(g0,g-4)
FEATURE [Sketcher::SketchObject] Sketch029  label="HoleLT"
  ExternalGeometry = -> [Pocket012]
  MapMode = 5
  Placement = pos=(0,65.4,0) rot=(0,0.707107,0.707107;3.14159rad)
  sketch-geometry (4):
    g0: LineSegment StartX=57.7 StartY=9.4 StartZ=0 EndX=60.5 EndY=9.4 EndZ=0
    g1: LineSegment StartX=60.5 StartY=9.4 StartZ=0 EndX=60.5 EndY=7 EndZ=0
    g2: LineSegment StartX=60.5 StartY=7 StartZ=0 EndX=57.7 EndY=7 EndZ=0
    g3: LineSegment StartX=57.7 StartY=7 StartZ=0 EndX=57.7 EndY=9.4 EndZ=0
  constraints (11):
    c: Coincident(g0,g1)
    c: Coincident(g1,g2)
    c: Coincident(g2,g3)
    c: Coincident(g3,g0)
    c: Horizontal(g0)
    c: Horizontal(g2)
    c: Vertical(g1)
    c: Vertical(g3)
    c: DistanceY(g1,g1) = 2.4
    c: Coincident(g1,g-4)
    c: PointOnObject(g0,g-3)
FEATURE [Sketcher::SketchObject] Sketch030  label="HoleRB"
  ExternalGeometry = -> [Pocket012]
  MapMode = 5
  Placement = pos=(0,-65.4,0) rot=(1,0,0;1.5708rad)
  Support = -> [Pocket012]
  sketch-geometry (4):
    g0: LineSegment StartX=57.7 StartY=9.4 StartZ=0 EndX=60.5 EndY=9.4 EndZ=0
    g1: LineSegment StartX=60.5 StartY=9.4 StartZ=0 EndX=60.5 EndY=7 EndZ=0
    g2: LineSegment StartX=60.5 StartY=7 StartZ=0 EndX=57.7 EndY=7 EndZ=0
    g3: LineSegment StartX=57.7 StartY=7 StartZ=0 EndX=57.7 EndY=9.4 EndZ=0
  constraints (11):
    c: Coincident(g0,g1)
    c: Coincident(g1,g2)
    c: Coincident(g2,g3)
    c: Coincident(g3,g0)
    c: Horizontal(g0)
    c: Horizontal(g2)
    c: Vertical(g1)
    c: Vertical(g3)
    c: Coincident(g1,g-4)
    c: PointOnObject(g0,g-3)
    c: DistanceY(g1,g1) = 2.4
FEATURE [PartDesign::Plane] DatumPlane  label="DatumPlane-HoleBottom"
  AttachmentOffset = pos=(0,0,-0.6) rot=(0,0,1;0rad)
  Length = 159.932
  MapMode = 5
  Placement = pos=(0,-64.8,-1e-16) rot=(1,0,0;1.5708rad)
  ResizeMode = 0
  Support = -> [Pocket012]
  Width = 33.4315
FEATURE [PartDesign::Plane] DatumPlane001  label="DatumPlane-HoleRT"
  AttachmentOffset = pos=(0,0,-0.6) rot=(0,0,1;0rad)
  Length = 159.932
  MapMode = 5
  Placement = pos=(0,62.8,1e-16) rot=(0,0.707107,0.707107;3.14159rad)
  ResizeMode = 0
  Support = -> [Pocket012]
  Width = 33.4315
FEATURE [PartDesign::Plane] DatumPlane002  label="DatumPlane-HoleLT"
  AttachmentOffset = pos=(0,0,-0.6) rot=(0,0,1;0rad)
  Length = 159.932
  MapMode = 5
  Placement = pos=(0,64.8,1e-16) rot=(0,0.707107,0.707107;3.14159rad)
  ResizeMode = 0
  Support = -> [Pocket012]
  Width = 33.4315
FEATURE [Sketcher::SketchObject] Sketch032  label="HoleLB2"
  ExternalGeometry = -> [Pocket012]
  MapMode = 5
  Placement = pos=(0,-64.8,-1e-16) rot=(1,0,0;1.5708rad)
  Support = -> [DatumPlane]
  sketch-geometry (4):
    g0: LineSegment StartX=-60.5 StartY=9 StartZ=0 EndX=-57.7 EndY=9 EndZ=0
    g1: LineSegment StartX=-57.7 StartY=9 StartZ=0 EndX=-57.7 EndY=7.4 EndZ=0
    g2: LineSegment StartX=-57.7 StartY=7.4 StartZ=0 EndX=-60.5 EndY=7.4 EndZ=0
    g3: LineSegment StartX=-60.5 StartY=7.4 StartZ=0 EndX=-60.5 EndY=9 EndZ=0
  constraints (12):
    c: Coincident(g0,g1)
    c: Coincident(g1,g2)
    c: Coincident(g2,g3)
    c: Coincident(g3,g0)
    c: Horizontal(g0)
    c: Horizontal(g2)
    c: Vertical(g1)
    c: Vertical(g3)
    c: DistanceY(g3,g3) = 1.6
    c: PointOnObject(g1,g-3)
    c: PointOnObject(g2,g-4)
    c: DistanceY(g-3,g1) = 0.4
FEATURE [Sketcher::SketchObject] Sketch033  label="HoleRB2"
  ExternalGeometry = -> [Sketch030]
  MapMode = 5
  Placement = pos=(0,-64.8,-1e-16) rot=(1,0,0;1.5708rad)
  Support = -> [DatumPlane]
  sketch-geometry (4):
    g0: LineSegment StartX=57.7 StartY=9 StartZ=0 EndX=60.5 EndY=9 EndZ=0
    g1: LineSegment StartX=60.5 StartY=9 StartZ=0 EndX=60.5 EndY=7.4 EndZ=0
    g2: LineSegment StartX=60.5 StartY=7.4 StartZ=0 EndX=57.7 EndY=7.4 EndZ=0
    g3: LineSegment StartX=57.7 StartY=7.4 StartZ=0 EndX=57.7 EndY=9 EndZ=0
  constraints (12):
    c: Coincident(g0,g1)
    c: Coincident(g1,g2)
    c: Coincident(g2,g3)
    c: Coincident(g3,g0)
    c: Horizontal(g0)
    c: Horizontal(g2)
    c: Vertical(g1)
    c: Vertical(g3)
    c: PointOnObject(g1,g-3)
    c: PointOnObject(g2,g-4)
    c: DistanceY(g-3,g1) = 0.4
    c: DistanceY(g1,g1) = 1.6
FEATURE [PartDesign::SubtractiveLoft] SubtractiveLoft  label="SubtractiveLB"
  BaseFeature = -> Pocket012
  Closed = false
  Profile = -> Sketch027
  Ruled = false
  Sections = -> [Sketch032]
FEATURE [PartDesign::SubtractiveLoft] SubtractiveLoft001  label="SubtractiveRB"
  BaseFeature = -> SubtractiveLoft
  Closed = false
  Profile = -> Sketch030
  Ruled = false
  Sections = -> [Sketch033]
FEATURE [Sketcher::SketchObject] Sketch034  label="HolleLT2"
  ExternalGeometry = -> [SubtractiveLoft001]
  MapMode = 5
  Placement = pos=(0,64.8,1e-16) rot=(0,0.707107,0.707107;3.14159rad)
  Support = -> [DatumPlane002]
  sketch-geometry (4):
    g0: LineSegment StartX=57.7 StartY=9 StartZ=0 EndX=60.5 EndY=9 EndZ=0
    g1: LineSegment StartX=60.5 StartY=9 StartZ=0 EndX=60.5 EndY=7.4 EndZ=0
    g2: LineSegment StartX=60.5 StartY=7.4 StartZ=0 EndX=57.7 EndY=7.4 EndZ=0
    g3: LineSegment StartX=57.7 StartY=7.4 StartZ=0 EndX=57.7 EndY=9 EndZ=0
  constraints (12):
    c: Coincident(g0,g1)
    c: Coincident(g1,g2)
    c: Coincident(g2,g3)
    c: Coincident(g3,g0)
    c: Horizontal(g0)
    c: Horizontal(g2)
    c: Vertical(g1)
    c: Vertical(g3)
    c: PointOnObject(g1,g-3)
    c: PointOnObject(g2,g-4)
    c: DistanceY(g1,g1) = 1.6
    c: DistanceY(g-3,g1) = 0.4
FEATURE [PartDesign::SubtractiveLoft] SubtractiveLoft002  label="SubtractiveLT"
  BaseFeature = -> SubtractiveLoft001
  Closed = false
  Profile = -> Sketch029
  Ruled = false
  Sections = -> [Sketch034]
FEATURE [PartDesign::Plane] DatumPlane003  label="DatumPlane-CoverB1"
  Length = 160.39
  MapMode = 5
  Placement = pos=(0,-65.6,0) rot=(0,0.707107,0.707107;3.14159rad)
  ResizeMode = 0
  Support = -> [Pad011]
  Width = 35.69
FEATURE [PartDesign::Plane] DatumPlane004  label="DatumPlane-CoverB2"
  AttachmentOffset = pos=(0,0,0.6) rot=(0,0,1;0rad)
  Length = 160.39
  MapMode = 5
  Placement = pos=(0,-65,-1e-16) rot=(0,0.707107,0.707107;3.14159rad)
  ResizeMode = 0
  Support = -> [DatumPlane003]
  Width = 35.69
FEATURE [PartDesign::Plane] DatumPlane005  label="DatumPlane-CoverLT2"
  AttachmentOffset = pos=(0,0,0.6) rot=(0,0,1;0rad)
  Length = 160.39
  MapMode = 5
  Placement = pos=(0,65,1e-16) rot=(1,0,0;1.5708rad)
  ResizeMode = 0
  Support = -> [Pad011]
  Width = 35.69
FEATURE [PartDesign::Plane] DatumPlane006  label="DatumPlane-CoverLT1"
  Length = 160.39
  MapMode = 5
  Placement = pos=(0,65.6,0) rot=(1,0,0;1.5708rad)
  ResizeMode = 0
  Support = -> [Pad011]
  Width = 35.69
FEATURE [PartDesign::Plane] DatumPlane007  label="DatumPlane-CoverRT1"
  Length = 160.39
  MapMode = 5
  Placement = pos=(0,63.6,0) rot=(1,0,0;1.5708rad)
  ResizeMode = 0
  Support = -> [Pad011]
  Width = 35.69
FEATURE [PartDesign::Plane] DatumPlane008  label="DatumPlane-CoverRT2"
  AttachmentOffset = pos=(0,0,0.6) rot=(0,0,1;0rad)
  Length = 160.39
  MapMode = 5
  Placement = pos=(0,63,1e-16) rot=(1,0,0;1.5708rad)
  ResizeMode = 0
  Support = -> [Pad011]
  Width = 35.69
FEATURE [Sketcher::SketchObject] Sketch044  label="HoleRT2"
  ExternalGeometry = -> [SubtractiveLoft002]
  MapMode = 5
  Placement = pos=(0,62.8,1e-16) rot=(0,0.707107,0.707107;3.14159rad)
  Support = -> [DatumPlane001]
  sketch-geometry (4):
    g0: LineSegment StartX=-88 StartY=9 StartZ=0 EndX=-85.2 EndY=9 EndZ=0
    g1: LineSegment StartX=-85.2 StartY=9 StartZ=0 EndX=-85.2 EndY=7.4 EndZ=0
    g2: LineSegment StartX=-85.2 StartY=7.4 StartZ=0 EndX=-88 EndY=7.4 EndZ=0
    g3: LineSegment StartX=-88 StartY=7.4 StartZ=0 EndX=-88 EndY=9 EndZ=0
  constraints (12):
    c: Coincident(g0,g1)
    c: Coincident(g1,g2)
    c: Coincident(g2,g3)
    c: Coincident(g3,g0)
    c: Horizontal(g0)
    c: Horizontal(g2)
    c: Vertical(g1)
    c: Vertical(g3)
    c: PointOnObject(g0,g-3)
    c: PointOnObject(g0,g-4)
    c: DistanceY(g3,g3) = 1.6
    c: DistanceY(g-3,g2) = 0.4
FEATURE [PartDesign::SubtractiveLoft] SubtractiveLoft003  label="SubtractiveRT"
  BaseFeature = -> SubtractiveLoft002
  Closed = false
  Profile = -> Sketch028
  Ruled = false
  Sections = -> [Sketch044]
FEATURE [Sketcher::SketchObject] Sketch045  label="LoftRB1"
  ExternalGeometry = -> [Pad011]
  MapMode = 5
  Placement = pos=(0,-65.6,0) rot=(0,0.707107,0.707107;3.14159rad)
  Support = -> [DatumPlane003]
  sketch-geometry (4):
    g0: LineSegment StartX=-60.5 StartY=-11.8 StartZ=0 EndX=-57.7 EndY=-11.8 EndZ=0
    g1: LineSegment StartX=-57.7 StartY=-11.8 StartZ=0 EndX=-57.7 EndY=-13.8 EndZ=0
    g2: LineSegment StartX=-57.7 StartY=-13.8 StartZ=0 EndX=-60.5 EndY=-13.8 EndZ=0
    g3: LineSegment StartX=-60.5 StartY=-13.8 StartZ=0 EndX=-60.5 EndY=-11.8 EndZ=0
  constraints (11):
    c: Coincident(g0,g1)
    c: Coincident(g1,g2)
    c: Coincident(g2,g3)
    c: Coincident(g3,g0)
    c: Horizontal(g0)
    c: Horizontal(g2)
    c: Vertical(g1)
    c: Vertical(g3)
    c: Coincident(g2,g-3)
    c: PointOnObject(g1,g-4)
    c: DistanceY(g1,g1) = 2
FEATURE [Sketcher::SketchObject] Sketch046  label="LoftRB2"
  ExternalGeometry = -> [Pad011]
  MapMode = 5
  Placement = pos=(0,-65,-1e-16) rot=(0,0.707107,0.707107;3.14159rad)
  Support = -> [DatumPlane004]
  sketch-geometry (4):
    g0: LineSegment StartX=-60.5 StartY=-12.2 StartZ=0 EndX=-57.7 EndY=-12.2 EndZ=0
    g1: LineSegment StartX=-57.7 StartY=-12.2 StartZ=0 EndX=-57.7 EndY=-13.4 EndZ=0
    g2: LineSegment StartX=-57.7 StartY=-13.4 StartZ=0 EndX=-60.5 EndY=-13.4 EndZ=0
    g3: LineSegment StartX=-60.5 StartY=-13.4 StartZ=0 EndX=-60.5 EndY=-12.2 EndZ=0
  constraints (12):
    c: Coincident(g0,g1)
    c: Coincident(g1,g2)
    c: Coincident(g2,g3)
    c: Coincident(g3,g0)
    c: Horizontal(g0)
    c: Horizontal(g2)
    c: Vertical(g1)
    c: Vertical(g3)
    c: PointOnObject(g2,g-3)
    c: PointOnObject(g1,g-4)
    c: DistanceY(g3,g3) = 1.2
    c: DistanceY(g-3,g2) = 0.4
FEATURE [Sketcher::SketchObject] Sketch047  label="LoftLB1"
  ExternalGeometry = -> [Pad011]
  MapMode = 5
  Placement = pos=(0,-65.6,0) rot=(0,0.707107,0.707107;3.14159rad)
  Support = -> [DatumPlane003]
  sketch-geometry (4):
    g0: LineSegment StartX=57.7 StartY=-11.8 StartZ=0 EndX=60.5 EndY=-11.8 EndZ=0
    g1: LineSegment StartX=60.5 StartY=-11.8 StartZ=0 EndX=60.5 EndY=-13.8 EndZ=0
    g2: LineSegment StartX=60.5 StartY=-13.8 StartZ=0 EndX=57.7 EndY=-13.8 EndZ=0
    g3: LineSegment StartX=57.7 StartY=-13.8 StartZ=0 EndX=57.7 EndY=-11.8 EndZ=0
  constraints (11):
    c: Coincident(g0,g1)
    c: Coincident(g1,g2)
    c: Coincident(g2,g3)
    c: Coincident(g3,g0)
    c: Horizontal(g0)
    c: Horizontal(g2)
    c: Vertical(g1)
    c: Vertical(g3)
    c: Coincident(g1,g-4)
    c: PointOnObject(g2,g-3)
    c: DistanceY(g1,g1) = 2
FEATURE [Sketcher::SketchObject] Sketch048  label="LoftLB2"
  ExternalGeometry = -> [Pad011]
  MapMode = 5
  Placement = pos=(0,-65,-1e-16) rot=(0,0.707107,0.707107;3.14159rad)
  Support = -> [DatumPlane004]
  sketch-geometry (4):
    g0: LineSegment StartX=57.7 StartY=-12.2 StartZ=0 EndX=60.5 EndY=-12.2 EndZ=0
    g1: LineSegment StartX=60.5 StartY=-12.2 StartZ=0 EndX=60.5 EndY=-13.4 EndZ=0
    g2: LineSegment StartX=60.5 StartY=-13.4 StartZ=0 EndX=57.7 EndY=-13.4 EndZ=0
    g3: LineSegment StartX=57.7 StartY=-13.4 StartZ=0 EndX=57.7 EndY=-12.2 EndZ=0
  constraints (12):
    c: Coincident(g0,g1)
    c: Coincident(g1,g2)
    c: Coincident(g2,g3)
    c: Coincident(g3,g0)
    c: Horizontal(g0)
    c: Horizontal(g2)
    c: Vertical(g1)
    c: Vertical(g3)
    c: PointOnObject(g0,g-3)
    c: PointOnObject(g0,g-4)
    c: DistanceY(g1,g1) = 1.2
    c: DistanceY(g-4,g1) = 0.4
FEATURE [Sketcher::SketchObject] Sketch049  label="LoftLT1"
  ExternalGeometry = -> [Pad011]
  MapMode = 5
  Placement = pos=(0,65.6,0) rot=(1,0,0;1.5708rad)
  Support = -> [DatumPlane006]
  sketch-geometry (4):
    g0: LineSegment StartX=-60.5 StartY=-11.8 StartZ=0 EndX=-57.7 EndY=-11.8 EndZ=0
    g1: LineSegment StartX=-57.7 StartY=-11.8 StartZ=0 EndX=-57.7 EndY=-13.8 EndZ=0
    g2: LineSegment StartX=-57.7 StartY=-13.8 StartZ=0 EndX=-60.5 EndY=-13.8 EndZ=0
    g3: LineSegment StartX=-60.5 StartY=-13.8 StartZ=0 EndX=-60.5 EndY=-11.8 EndZ=0
  constraints (11):
    c: Coincident(g0,g1)
    c: Coincident(g1,g2)
    c: Coincident(g2,g3)
    c: Coincident(g3,g0)
    c: Horizontal(g0)
    c: Horizontal(g2)
    c: Vertical(g1)
    c: Vertical(g3)
    c: Coincident(g1,g-4)
    c: PointOnObject(g2,g-3)
    c: DistanceY(g3,g3) = 2
FEATURE [Sketcher::SketchObject] Sketch050  label="LoftLT2"
  ExternalGeometry = -> [Pad011]
  MapMode = 5
  Placement = pos=(0,65,1e-16) rot=(1,0,0;1.5708rad)
  Support = -> [DatumPlane005]
  sketch-geometry (4):
    g0: LineSegment StartX=-60.5 StartY=-12.2 StartZ=0 EndX=-57.7 EndY=-12.2 EndZ=0
    g1: LineSegment StartX=-57.7 StartY=-12.2 StartZ=0 EndX=-57.7 EndY=-13.4 EndZ=0
    g2: LineSegment StartX=-57.7 StartY=-13.4 StartZ=0 EndX=-60.5 EndY=-13.4 EndZ=0
    g3: LineSegment StartX=-60.5 StartY=-13.4 StartZ=0 EndX=-60.5 EndY=-12.2 EndZ=0
  constraints (12):
    c: Coincident(g0,g1)
    c: Coincident(g1,g2)
    c: Coincident(g2,g3)
    c: Coincident(g3,g0)
    c: Horizontal(g0)
    c: Horizontal(g2)
    c: Vertical(g1)
    c: Vertical(g3)
    c: PointOnObject(g2,g-3)
    c: PointOnObject(g1,g-4)
    c: DistanceY(g3,g3) = 1.2
    c: DistanceY(g-3,g2) = 0.4
FEATURE [Sketcher::SketchObject] Sketch051  label="LoftRT1"
  ExternalGeometry = -> [Pad011]
  MapMode = 5
  Placement = pos=(0,63.6,0) rot=(1,0,0;1.5708rad)
  Support = -> [DatumPlane007]
  sketch-geometry (4):
    g0: LineSegment StartX=85.2 StartY=-11.8 StartZ=0 EndX=88 EndY=-11.8 EndZ=0
    g1: LineSegment StartX=88 StartY=-11.8 StartZ=0 EndX=88 EndY=-13.8 EndZ=0
    g2: LineSegment StartX=88 StartY=-13.8 StartZ=0 EndX=85.2 EndY=-13.8 EndZ=0
    g3: LineSegment StartX=85.2 StartY=-13.8 StartZ=0 EndX=85.2 EndY=-11.8 EndZ=0
  constraints (11):
    c: Coincident(g0,g1)
    c: Coincident(g1,g2)
    c: Coincident(g2,g3)
    c: Coincident(g3,g0)
    c: Horizontal(g0)
    c: Horizontal(g2)
    c: Vertical(g1)
    c: Vertical(g3)
    c: Coincident(g-4,g1)
    c: PointOnObject(g2,g-3)
    c: DistanceY(g1,g1) = 2
FEATURE [Sketcher::SketchObject] Sketch052  label="LoftRT2"
  ExternalGeometry = -> [Pad011]
  MapMode = 5
  Placement = pos=(0,63,1e-16) rot=(1,0,0;1.5708rad)
  Support = -> [DatumPlane008]
  sketch-geometry (4):
    g0: LineSegment StartX=85.2 StartY=-12.2 StartZ=0 EndX=88 EndY=-12.2 EndZ=0
    g1: LineSegment StartX=88 StartY=-12.2 StartZ=0 EndX=88 EndY=-13.4 EndZ=0
    g2: LineSegment StartX=88 StartY=-13.4 StartZ=0 EndX=85.2 EndY=-13.4 EndZ=0
    g3: LineSegment StartX=85.2 StartY=-13.4 StartZ=0 EndX=85.2 EndY=-12.2 EndZ=0
  constraints (12):
    c: Coincident(g0,g1)
    c: Coincident(g1,g2)
    c: Coincident(g2,g3)
    c: Coincident(g3,g0)
    c: Horizontal(g0)
    c: Horizontal(g2)
    c: Vertical(g1)
    c: Vertical(g3)
    c: PointOnObject(g0,g-4)
    c: PointOnObject(g0,g-3)
    c: DistanceY(g1,g1) = 1.2
    c: DistanceY(g-4,g1) = 0.4
FEATURE [PartDesign::AdditiveLoft] AdditiveLoft
  BaseFeature = -> Pad011
  Closed = false
  Profile = -> Sketch045
  Ruled = false
  Sections = -> [Sketch046]
FEATURE [PartDesign::AdditiveLoft] AdditiveLoft001
  BaseFeature = -> AdditiveLoft
  Closed = false
  Profile = -> Sketch047
  Ruled = false
  Sections = -> [Sketch048]
FEATURE [PartDesign::AdditiveLoft] AdditiveLoft002
  BaseFeature = -> AdditiveLoft001
  Closed = false
  Profile = -> Sketch049
  Ruled = false
  Sections = -> [Sketch050]
FEATURE [PartDesign::AdditiveLoft] AdditiveLoft003
  BaseFeature = -> AdditiveLoft002
  Closed = false
  Profile = -> Sketch051
  Ruled = false
  Sections = -> [Sketch052]
FEATURE [PartDesign::Chamfer] Chamfer
  Base = -> SubtractiveLoft003 [Edge237,Edge239,Edge214,Edge216]
  BaseFeature = -> SubtractiveLoft003
  Size = 1
FEATURE [Sketcher::SketchObject] Sketch053
  ExternalGeometry = -> [Chamfer]
  MapMode = 5
  Placement = pos=(0,0,6) rot=(0,0,1;0rad)
  Support = -> [Chamfer]
  sketch-geometry (4):
    g0: Circle CenterX=-14 CenterY=69.1 CenterZ=0 NormalX=0 NormalY=0 NormalZ=1 AngleXU=0 Radius=1.2
    g1: Circle CenterX=-14 CenterY=17.4 CenterZ=0 NormalX=0 NormalY=0 NormalZ=1 AngleXU=0 Radius=1.2
    g2: Circle CenterX=82 CenterY=17.4 CenterZ=0 NormalX=0 NormalY=0 NormalZ=1 AngleXU=0 Radius=1.2
    g3: Circle CenterX=82 CenterY=69.1 CenterZ=0 NormalX=0 NormalY=0 NormalZ=1 AngleXU=0 Radius=1.2
  constraints (12):
    c: Equal(g1,g0)
    c: Equal(g0,g3)
    c: Equal(g3,g2)
    c: Vertical(g1,g0)
    c: Horizontal(g0,g3)
    c: Horizontal(g1,g2)
    c: Vertical(g2,g3)
    c: Radius(g0) = 1.2
    c: DistanceX(g-3,g0) = 3
    c: DistanceX(g3,g-5) = 3
    c: DistanceY(g-4,g1) = 3.4
    c: DistanceY(g0,g-3) = 3.4
FEATURE [PartDesign::Pocket] Pocket013
  BaseFeature = -> Chamfer
  Length = 4
  Length2 = 100
  Profile = -> Sketch053
  Type = 0
FEATURE [Sketcher::SketchObject] Sketch054
  MapMode = 5
  Support = -> [XY_Plane005]
  sketch-geometry (4):
    g0: LineSegment StartX=0 StartY=12 StartZ=0 EndX=6.6 EndY=12 EndZ=0
    g1: LineSegment StartX=6.6 StartY=12 StartZ=0 EndX=6.6 EndY=0 EndZ=0
    g2: LineSegment StartX=6.6 StartY=0 StartZ=0 EndX=0 EndY=0 EndZ=0
    g3: LineSegment StartX=0 StartY=0 StartZ=0 EndX=0 EndY=12 EndZ=0
  constraints (11):
    c: Coincident(g0,g1)
    c: Coincident(g1,g2)
    c: Coincident(g2,g3)
    c: Coincident(g3,g0)
    c: Horizontal(g0)
    c: Vertical(g1)
    c: Vertical(g3)
    c: Horizontal(g2)
    c: Coincident(g2,g-1)
    c: DistanceY(g1,g1) = 12
    c: DistanceX(g2,g2) = 6.6
FEATURE [PartDesign::Pad] Pad012
  Length = 2
  Length2 = 100
  Profile = -> Sketch054
  Type = 0
FEATURE [Sketcher::SketchObject] Sketch055
  ExternalGeometry = -> [Pad012]
  MapMode = 5
  Placement = pos=(0,0,2) rot=(0,0,1;0rad)
  Support = -> [Pad012]
  sketch-geometry (4):
    g0: LineSegment StartX=0 StartY=12 StartZ=0 EndX=6.6 EndY=12 EndZ=0
    g1: LineSegment StartX=6.6 StartY=12 StartZ=0 EndX=6.6 EndY=7 EndZ=0
    g2: LineSegment StartX=6.6 StartY=7 StartZ=0 EndX=0 EndY=7 EndZ=0
    g3: LineSegment StartX=0 StartY=7 StartZ=0 EndX=0 EndY=12 EndZ=0
  constraints (10):
    c: Coincident(g0,g1)
    c: Coincident(g1,g2)
    c: Coincident(g2,g3)
    c: Coincident(g3,g0)
    c: Horizontal(g2)
    c: Vertical(g1)
    c: Vertical(g3)
    c: Coincident(g0,g-3)
    c: Coincident(g0,g-3)
    c: DistanceY(g-1,g2) = 7
FEATURE [PartDesign::Pad] Pad013
  BaseFeature = -> Pad012
  Length = 0.8
  Length2 = 100
  Profile = -> Sketch055
  Type = 0
FEATURE [Sketcher::SketchObject] Sketch056
  ExternalGeometry = -> [Pad013]
  MapMode = 5
  Placement = pos=(0,0,2) rot=(0,0,1;0rad)
  Support = -> [Pad013]
  sketch-geometry (1):
    g0: Circle CenterX=3 CenterY=3.4 CenterZ=0 NormalX=0 NormalY=0 NormalZ=1 AngleXU=0 Radius=1.8
  constraints (3):
    c: Radius(g0) = 1.8
    c: DistanceX(g-1,g0) = 3
    c: DistanceY(g-1,g0) = 3.4
FEATURE [PartDesign::Pocket] Pocket014
  BaseFeature = -> Pad013
  Length = 2
  Length2 = 100
  Profile = -> Sketch056
  Type = 0
FEATURE [PartDesign::Body] Body005
  Group = -> [Sketch054,Pad012,Sketch055,Pad013,Sketch056,Pocket014]
  Origin = -> Origin005
  Placement = pos=(-17,72.5,8) rot=(1,0,0;3.14159rad)
  Tip = -> Pocket014
FEATURE [Sketcher::SketchObject] Sketch057
  MapMode = 5
  Placement = pos=(0,-81.4,0) rot=(1,0,0;1.5708rad)
  Support = -> [Pocket013]
  sketch-geometry (2):
    g0: Circle CenterX=-2 CenterY=4 CenterZ=0 NormalX=0 NormalY=0 NormalZ=1 AngleXU=0 Radius=1.2
    g1: Circle CenterX=2 CenterY=4 CenterZ=0 NormalX=0 NormalY=0 NormalZ=1 AngleXU=0 Radius=1.2
  constraints (6):
    c: Horizontal(g0,g1)
    c: Equal(g1,g0)
    c: Radius(g1) = 1.2
    c: DistanceY(g-1,g1) = 4
    c: DistanceX(g-1,g1) = 2
    c: DistanceX(g0,g-1) = 2
FEATURE [PartDesign::Pocket] Pocket015
  BaseFeature = -> Pocket013
  Length = 3
  Length2 = 100
  Profile = -> Sketch057
  Type = 0
FEATURE [PartDesign::Chamfer] Chamfer003
  Base = -> AdditiveLoft003 [Edge59,Edge70]
  BaseFeature = -> AdditiveLoft003
  Size = 1.4
FEATURE [PartDesign::Chamfer] Chamfer004
  Base = -> Chamfer003 [Edge53]
  BaseFeature = -> Chamfer003
  Size = 1
FEATURE [PartDesign::Body] Body002  label="Cover"
  Group = -> [ShapeBinder004,ShapeBinder005,Sketch014,Pad007,Sketch017,Pocket006,Sketch018,Pocket007,Sketch022,Pocket009,Sketch023,Pocket010,Sketch026,Pad011,DatumPlane003,DatumPlane004,DatumPlane005,DatumPlane006,DatumPlane007,DatumPlane008,Sketch045,Sketch046,Sketch047,Sketch048,Sketch049,Sketch050,Sketch051,Sketch052,AdditiveLoft,AdditiveLoft001,AdditiveLoft002,AdditiveLoft003,Chamfer003,Chamfer004]
  Origin = -> Origin002
  Placement = pos=(0,0,21) rot=(0,0,1;0rad)
  Tip = -> Chamfer004
FEATURE [PartDesign::ShapeBinder] ShapeBinder006
  Support = -> [Sketch]
  TraceSupport = false
FEATURE [PartDesign::ShapeBinder] ShapeBinder007
  Support = -> [Sketch001]
  TraceSupport = false
FEATURE [Sketcher::SketchObject] Sketch059
  ExternalGeometry = -> [ShapeBinder006,ShapeBinder007]
  MapMode = 5
  Support = -> [XY_Plane006]
  sketch-geometry (7):
    g0: LineSegment StartX=61 StartY=137.4 StartZ=0 EndX=79 EndY=137.4 EndZ=0
    g1: LineSegment StartX=85 StartY=131.4 StartZ=0 EndX=85 EndY=79.645 EndZ=0
    g2: LineSegment StartX=80 StartY=81.4 StartZ=0 EndX=55 EndY=81.4 EndZ=0
    g3: LineSegment StartX=55 StartY=81.4 StartZ=0 EndX=55 EndY=131.4 EndZ=0
    g4: ArcOfCircle CenterX=61 CenterY=131.4 CenterZ=0 NormalX=0 NormalY=0 NormalZ=1 AngleXU=0 Radius=6 StartAngle=1.5708 EndAngle=3.14159
    g5: ArcOfCircle CenterX=79 CenterY=131.4 CenterZ=0 NormalX=0 NormalY=0 NormalZ=1 AngleXU=0 Radius=6 StartAngle=-1.8e-15 EndAngle=1.5708
    g6: ArcOfCircle CenterX=80 CenterY=73.4 CenterZ=0 NormalX=0 NormalY=0 NormalZ=1 AngleXU=0 Radius=8 StartAngle=0.895665 EndAngle=1.5708
  constraints (20):
    c: Horizontal(g0)
    c: Horizontal(g2)
    c: Vertical(g1)
    c: Vertical(g3)
    c: Tangent(g0,g4) = 1.5708
    c: Tangent(g3,g4) = 1.5708
    c: Tangent(g0,g5) = 1.5708
    c: Tangent(g1,g5) = 1.5708
    c: Coincident(g2,g3)
    c: Horizontal(g4,g5)
    c: DistanceY(g-3,g2) = 3
    c: DistanceX(g5,g1) = 6
    c: Radius(g6) = 8
    c: Coincident(g6,g1)
    c: Coincident(g2,g6)
    c: DistanceY(g3,g3) = 50
    c: Vertical(g6,g2)
    c: DistanceX(g0,g0) = 18
    c: Vertical(g-4,g1)
    c: DistanceX(g6,g-4) = 5
FEATURE [PartDesign::Pad] Pad014
  Length = 14
  Length2 = 100
  Profile = -> Sketch059
  Type = 0
FEATURE [PartDesign::Plane] DatumPlane009  label="Inner-Bottom"
  AttachmentOffset = pos=(0,0,2) rot=(0,0,1;0rad)
  Length = 118.667
  MapMode = 2
  Placement = pos=(0,0,2) rot=(0,0,1;0rad)
  ResizeMode = 0
  Support = -> [ShapeBinder006]
  Width = 171.067
FEATURE [Sketcher::SketchObject] Sketch060
  ExternalGeometry = -> [Pad014]
  MapMode = 5
  Placement = pos=(0,0,2) rot=(0,0,1;0rad)
  Support = -> [DatumPlane009]
  sketch-geometry (6):
    g0: LineSegment StartX=61 StartY=135.4 StartZ=0 EndX=79 EndY=135.4 EndZ=0
    g1: LineSegment StartX=83 StartY=131.4 StartZ=0 EndX=83 EndY=83.4 EndZ=0
    g2: LineSegment StartX=83 StartY=83.4 StartZ=0 EndX=57 EndY=83.4 EndZ=0
    g3: LineSegment StartX=57 StartY=83.4 StartZ=0 EndX=57 EndY=131.4 EndZ=0
    g4: ArcOfCircle CenterX=61 CenterY=131.4 CenterZ=0 NormalX=0 NormalY=0 NormalZ=1 AngleXU=0 Radius=4 StartAngle=1.5708 EndAngle=3.14159
    g5: ArcOfCircle CenterX=79 CenterY=131.4 CenterZ=0 NormalX=0 NormalY=0 NormalZ=1 AngleXU=0 Radius=4 StartAngle=-9e-16 EndAngle=1.5708
  constraints (20):
    c: Coincident(g0,g5)
    c: Coincident(g2,g3)
    c: Coincident(g3,g4)
    c: Coincident(g1,g2)
    c: Coincident(g1,g5)
    c: Coincident(g0,g4)
    c: Horizontal(g0)
    c: Vertical(g1)
    c: Vertical(g3)
    c: Horizontal(g2)
    c: Horizontal(g4,g5)
    c: Horizontal(g3,g4)
    c: Horizontal(g5,g1)
    c: Vertical(g5,g0)
    c: Vertical(g0,g4)
    c: DistanceY(g5,g0) = 4
    c: DistanceX(g-3,g2) = 2
    c: DistanceY(g-3,g2) = 2
    c: DistanceX(g2,g2) = 26
    c: DistanceY(g1,g1) = 48
FEATURE [Sketcher::SketchObject] Sketch062  label="Antenna-Outline"
  MapMode = 5
  Support = -> [XY_Plane]
FEATURE [PartDesign::Body] Body  label="Sketch"
  Group = -> [Sketch,Sketch001,Sketch062]
  Origin = -> Origin
FEATURE [PartDesign::Pocket] Pocket017
  BaseFeature = -> Pad014
  Length = 12
  Length2 = 100
  Profile = -> Sketch060
  Reversed = true
  Type = 0
FEATURE [Sketcher::SketchObject] Sketch063
  ExternalGeometry = -> [Pocket017]
  MapMode = 5
  Placement = pos=(0,0,14) rot=(0,0,1;0rad)
  Support = -> [Pocket017]
  sketch-geometry (6):
    g0: LineSegment StartX=61 StartY=137.4 StartZ=0 EndX=79 EndY=137.4 EndZ=0
    g1: LineSegment StartX=85 StartY=131.4 StartZ=0 EndX=85 EndY=83.4 EndZ=0
    g2: LineSegment StartX=85 StartY=83.4 StartZ=0 EndX=55 EndY=83.4 EndZ=0
    g3: LineSegment StartX=55 StartY=83.4 StartZ=0 EndX=55 EndY=131.4 EndZ=0
    g4: ArcOfCircle CenterX=79 CenterY=131.4 CenterZ=0 NormalX=0 NormalY=0 NormalZ=1 AngleXU=0 Radius=6 StartAngle=0 EndAngle=1.5708
    g5: ArcOfCircle CenterX=61 CenterY=131.4 CenterZ=0 NormalX=0 NormalY=0 NormalZ=1 AngleXU=0 Radius=6 StartAngle=1.5708 EndAngle=3.14159
  constraints (16):
    c: Coincident(g1,g2)
    c: Coincident(g2,g3)
    c: Horizontal(g0)
    c: Horizontal(g2)
    c: Vertical(g1)
    c: Vertical(g3)
    c: Tangent(g0,g4) = 1.5708
    c: Tangent(g1,g4) = 1.5708
    c: Tangent(g0,g5) = 1.5708
    c: Tangent(g3,g5) = 1.5708
    c: Horizontal(g5,g4)
    c: PointOnObject(g2,g-3)
    c: PointOnObject(g1,g-6)
    c: Horizontal(g1,g-5)
    c: Horizontal(g5,g-3)
    c: DistanceY(g4,g0) = 6
FEATURE [PartDesign::Pocket] Pocket018
  BaseFeature = -> Pocket017
  Length = 6
  Length2 = 100
  Profile = -> Sketch063
  Type = 0
FEATURE [Sketcher::SketchObject] Sketch064
  ExternalGeometry = -> [Pocket018]
  MapMode = 5
  Placement = pos=(0,0,2) rot=(0,0,1;0rad)
  Support = -> [Pocket018]
  sketch-geometry (1):
    g0: Circle CenterX=70 CenterY=98.4 CenterZ=0 NormalX=0 NormalY=0 NormalZ=1 AngleXU=0 Radius=4
  constraints (3):
    c: DistanceY(g-3,g0) = 15
    c: DistanceX(g-3,g0) = 13
    c: Radius(g0) = 4
FEATURE [PartDesign::Pad] Pad015
  BaseFeature = -> Pocket018
  Length = 3
  Length2 = 100
  Profile = -> Sketch064
  Type = 0
FEATURE [Sketcher::SketchObject] Sketch065
  ExternalGeometry = -> [Pad015]
  MapMode = 5
  Placement = pos=(0,0,5) rot=(0,0,1;0rad)
  Support = -> [Pad015]
  sketch-geometry (1):
    g0: Circle CenterX=70 CenterY=98.4 CenterZ=0 NormalX=0 NormalY=0 NormalZ=1 AngleXU=0 Radius=1.8
  constraints (2):
    c: Coincident(g0,g-3)
    c: Radius(g0) = 1.8
FEATURE [PartDesign::Pocket] Pocket019
  BaseFeature = -> Pad015
  Length = 5
  Length2 = 100
  Profile = -> Sketch065
  Type = 1
FEATURE [PartDesign::ShapeBinder] ShapeBinder008
  Support = -> [Sketch]
  TraceSupport = false
FEATURE [PartDesign::ShapeBinder] ShapeBinder009
  Support = -> [Sketch001]
  TraceSupport = false
FEATURE [PartDesign::Plane] DatumPlane010
  Length = 118.667
  MapMode = 2
  Placement = pos=(0,0,14) rot=(0,0,1;0rad)
  ResizeMode = 0
  Width = 171.067
FEATURE [Sketcher::SketchObject] Sketch066
  ExternalGeometry = -> [ShapeBinder008,ShapeBinder009]
  MapMode = 5
  Placement = pos=(0,0,14) rot=(0,0,1;0rad)
  Support = -> [DatumPlane010]
  sketch-geometry (6):
    g0: LineSegment StartX=61 StartY=137.4 StartZ=0 EndX=79 EndY=137.4 EndZ=0
    g1: LineSegment StartX=85 StartY=131.4 StartZ=0 EndX=85 EndY=83.6 EndZ=0
    g2: LineSegment StartX=85 StartY=83.6 StartZ=0 EndX=55 EndY=83.6 EndZ=0
    g3: LineSegment StartX=55 StartY=83.6 StartZ=0 EndX=55 EndY=131.4 EndZ=0
    g4: ArcOfCircle CenterX=79 CenterY=131.4 CenterZ=0 NormalX=0 NormalY=0 NormalZ=1 AngleXU=0 Radius=6 StartAngle=5e-16 EndAngle=1.5708
    g5: ArcOfCircle CenterX=61 CenterY=131.4 CenterZ=0 NormalX=0 NormalY=0 NormalZ=1 AngleXU=0 Radius=6 StartAngle=1.5708 EndAngle=3.14159
  constraints (16):
    c: Coincident(g2,g3)
    c: Horizontal(g0)
    c: Horizontal(g2)
    c: Vertical(g1)
    c: Vertical(g3)
    c: Tangent(g0,g4) = 1.5708
    c: Tangent(g1,g4) = 1.5708
    c: Tangent(g0,g5) = 1.5708
    c: Tangent(g3,g5) = 1.5708
    c: DistanceY(g-3,g2) = 5.2
    c: DistanceY(g3,g3) = 47.8
    c: DistanceX(g0,g0) = 18
    c: DistanceY(g4,g0) = 6
    c: Horizontal(g5,g4)
    c: Vertical(g-4,g1)
    c: Coincident(g1,g2)
FEATURE [PartDesign::Pad] Pad016
  Length = 5.8
  Length2 = 100
  Placement = pos=(0,0,14) rot=(0,0,1;0rad)
  Profile = -> Sketch066
  Reversed = true
  Type = 0
FEATURE [Sketcher::SketchObject] Sketch067
  ExternalGeometry = -> [Pad016]
  MapMode = 5
  Placement = pos=(0,0,8.2) rot=(1,0,0;3.14159rad)
  Support = -> [Pad016]
  sketch-geometry (6):
    g0: LineSegment StartX=57 StartY=-83.6 StartZ=0 EndX=83 EndY=-83.6 EndZ=0
    g1: LineSegment StartX=83 StartY=-83.6 StartZ=0 EndX=83 EndY=-131.4 EndZ=0
    g2: LineSegment StartX=79 StartY=-135.4 StartZ=0 EndX=61 EndY=-135.4 EndZ=0
    g3: LineSegment StartX=57 StartY=-131.4 StartZ=0 EndX=57 EndY=-83.6 EndZ=0
    g4: ArcOfCircle CenterX=79 CenterY=-131.4 CenterZ=0 NormalX=0 NormalY=0 NormalZ=1 AngleXU=0 Radius=4 StartAngle=4.71239 EndAngle=6.28319
    g5: ArcOfCircle CenterX=61 CenterY=-131.4 CenterZ=0 NormalX=0 NormalY=0 NormalZ=1 AngleXU=0 Radius=4 StartAngle=3.14159 EndAngle=4.71239
  constraints (16):
    c: Coincident(g0,g1)
    c: Coincident(g3,g0)
    c: Horizontal(g0)
    c: Horizontal(g2)
    c: Vertical(g1)
    c: Vertical(g3)
    c: Tangent(g1,g4) = 1.5708
    c: Tangent(g2,g4) = 1.5708
    c: Tangent(g2,g5) = 1.5708
    c: Tangent(g3,g5) = 1.5708
    c: Horizontal(g5,g4)
    c: DistanceX(g3,g5) = 4
    c: Horizontal(g-4,g0)
    c: DistanceX(g-4,g0) = 2
    c: DistanceX(g0,g-3) = 2
    c: Horizontal(g-4,g3)
FEATURE [PartDesign::Pocket] Pocket020
  BaseFeature = -> Pad016
  Length = 3.8
  Length2 = 100
  Placement = pos=(0,0,14) rot=(0,0,1;0rad)
  Profile = -> Sketch067
  Type = 0
FEATURE [Sketcher::SketchObject] Sketch068
  ExternalGeometry = -> [Pocket020]
  MapMode = 5
  Placement = pos=(0,0,12) rot=(1,0,0;3.14159rad)
  Support = -> [Pocket020]
  sketch-geometry (1):
    g0: Circle CenterX=70 CenterY=-98.4 CenterZ=0 NormalX=0 NormalY=0 NormalZ=1 AngleXU=0 Radius=4
  constraints (3):
    c: Radius(g0) = 4
    c: DistanceX(g0,g-3) = 13
    c: DistanceY(g0,g-3) = 14.8
FEATURE [PartDesign::Pad] Pad017
  BaseFeature = -> Pocket020
  Length = 6.8
  Length2 = 100
  Placement = pos=(0,0,14) rot=(0,0,1;0rad)
  Profile = -> Sketch068
  Type = 0
FEATURE [Sketcher::SketchObject] Sketch069
  ExternalGeometry = -> [Pad017]
  MapMode = 5
  Placement = pos=(0,0,5.2) rot=(1,0,0;3.14159rad)
  Support = -> [Pad017]
  sketch-geometry (1):
    g0: Circle CenterX=70 CenterY=-98.4 CenterZ=0 NormalX=0 NormalY=0 NormalZ=1 AngleXU=0 Radius=1.2
  constraints (2):
    c: Coincident(g0,g-3)
    c: Radius(g0) = 1.2
FEATURE [PartDesign::Pocket] Pocket021
  BaseFeature = -> Pad017
  Length = 5
  Length2 = 100
  Placement = pos=(0,0,14) rot=(0,0,1;0rad)
  Profile = -> Sketch069
  Type = 0
FEATURE [Sketcher::SketchObject] Sketch070
  ExternalGeometry = -> [Pocket019]
  MapMode = 5
  Placement = pos=(0,81.4,0) rot=(1,0,0;1.5708rad)
  sketch-geometry (5):
    g0: Circle CenterX=63 CenterY=6 CenterZ=0 NormalX=0 NormalY=0 NormalZ=1 AngleXU=0 Radius=1.8
    g1: LineSegment StartX=70 StartY=9 StartZ=0 EndX=80 EndY=9 EndZ=0
    g2: LineSegment StartX=80 StartY=9 StartZ=0 EndX=80 EndY=5 EndZ=0
    g3: LineSegment StartX=80 StartY=5 StartZ=0 EndX=70 EndY=5 EndZ=0
    g4: LineSegment StartX=70 StartY=5 StartZ=0 EndX=70 EndY=9 EndZ=0
  constraints (15):
    c: Coincident(g1,g2)
    c: Coincident(g2,g3)
    c: Coincident(g3,g4)
    c: Coincident(g4,g1)
    c: Horizontal(g1)
    c: Horizontal(g3)
    c: Vertical(g2)
    c: Vertical(g4)
    c: DistanceX(g1,g1) = 10
    c: DistanceY(g2,g2) = 4
    c: Radius(g0) = 1.8
    c: DistanceX(g-3,g0) = 8
    c: DistanceY(g-3,g0) = 6
    c: DistanceX(g-3,g3) = 15
    c: DistanceY(g-3,g3) = 5
FEATURE [PartDesign::Fillet] Fillet002
  Base = -> Pocket021 [Edge37]
  BaseFeature = -> Pocket021
  Placement = pos=(0,0,14) rot=(0,0,1;0rad)
  Radius = 2
FEATURE [PartDesign::Body] Body007  label="Antenna-Cover"
  Group = -> [ShapeBinder008,ShapeBinder009,DatumPlane010,Sketch066,Pad016,Sketch067,Pocket020,Sketch068,Pad017,Sketch069,Pocket021,Fillet002]
  Origin = -> Origin007
  Tip = -> Fillet002
FEATURE [PartDesign::Pocket] Pocket022
  BaseFeature = -> Pocket019
  Length = 2
  Length2 = 100
  Profile = -> Sketch070
  Type = 0
FEATURE [Sketcher::SketchObject] Sketch071
  ExternalGeometry = -> [Pocket022]
  MapMode = 5
  Placement = pos=(0,0,0) rot=(1,0,0;3.14159rad)
  Support = -> [Pocket022]
  sketch-geometry (1):
    g0: Circle CenterX=70 CenterY=-98.4 CenterZ=0 NormalX=0 NormalY=0 NormalZ=1 AngleXU=0 Radius=3.2
  constraints (2):
    c: Coincident(g0,g-3)
    c: Radius(g0) = 3.2
FEATURE [PartDesign::Pocket] Pocket023
  BaseFeature = -> Pocket022
  Length = 2
  Length2 = 100
  Profile = -> Sketch071
  Type = 0
FEATURE [PartDesign::Fillet] Fillet003
  Base = -> Pocket023 [Edge74]
  BaseFeature = -> Pocket023
  Radius = 2
FEATURE [PartDesign::Body] Body006  label="Antenna-Bottom"
  Group = -> [ShapeBinder006,ShapeBinder007,Sketch059,Pad014,DatumPlane009,Sketch060,Pocket017,Sketch063,Pocket018,Sketch064,Pad015,Sketch065,Pocket019,Sketch070,Pocket022,Sketch071,Pocket023,Fillet003]
  Origin = -> Origin006
  Tip = -> Fillet003
FEATURE [Sketcher::SketchObject] Sketch072
  MapMode = 5
  Placement = pos=(0,78.6,0) rot=(1,0,0;1.5708rad)
  Support = -> [Pocket015]
  sketch-geometry (5):
    g0: Circle CenterX=63 CenterY=6 CenterZ=0 NormalX=0 NormalY=0 NormalZ=1 AngleXU=0 Radius=1.8
    g1: LineSegment StartX=70 StartY=7 StartZ=0 EndX=80 EndY=7 EndZ=0
    g2: LineSegment StartX=80 StartY=7 StartZ=0 EndX=80 EndY=5 EndZ=0
    g3: LineSegment StartX=80 StartY=5 StartZ=0 EndX=70 EndY=5 EndZ=0
    g4: LineSegment StartX=70 StartY=5 StartZ=0 EndX=70 EndY=7 EndZ=0
  constraints (15):
    c: DistanceX(g-1,g0) = 63
    c: DistanceY(g-1,g0) = 6
    c: Radius(g0) = 1.8
    c: Coincident(g1,g2)
    c: Coincident(g2,g3)
    c: Coincident(g3,g4)
    c: Coincident(g4,g1)
    c: Horizontal(g1)
    c: Horizontal(g3)
    c: Vertical(g2)
    c: Vertical(g4)
    c: DistanceX(g1,g1) = 10
    c: DistanceY(g2,g2) = 2
    c: DistanceX(g-1,g3) = 70
    c: DistanceY(g-1,g3) = 5
FEATURE [PartDesign::Pocket] Pocket024
  BaseFeature = -> Pocket015
  Length = 3
  Length2 = 100
  Profile = -> Sketch072
  Type = 0
FEATURE [Sketcher::SketchObject] Sketch073
  ExternalGeometry = -> [Pocket024]
  MapMode = 5
  Placement = pos=(0,0,4) rot=(0,0,1;0rad)
  Support = -> [Pocket024]
  sketch-geometry (4):
    g0: LineSegment StartX=-12.75 StartY=62.5 StartZ=0 EndX=-10.75 EndY=62.5 EndZ=0
    g1: LineSegment StartX=-10.75 StartY=62.5 StartZ=0 EndX=-10.75 EndY=24 EndZ=0
    g2: LineSegment StartX=-10.75 StartY=24 StartZ=0 EndX=-12.75 EndY=24 EndZ=0
    g3: LineSegment StartX=-12.75 StartY=24 StartZ=0 EndX=-12.75 EndY=62.5 EndZ=0
  constraints (12):
    c: Coincident(g0,g1)
    c: Coincident(g1,g2)
    c: Coincident(g2,g3)
    c: Coincident(g3,g0)
    c: Horizontal(g0)
    c: Horizontal(g2)
    c: Vertical(g1)
    c: Vertical(g3)
    c: PointOnObject(g0,g-5)
    c: DistanceY(g0,g-3) = 10
    c: DistanceY(g-4,g2) = 10
    c: DistanceX(g0,g0) = 2
FEATURE [PartDesign::Pocket] Pocket025
  BaseFeature = -> Pocket024
  Length = 1.2
  Length2 = 100
  Profile = -> Sketch073
  Type = 0
FEATURE [PartDesign::Chamfer] Chamfer005
  Base = -> Pocket025 [Edge209,Edge225]
  BaseFeature = -> Pocket025
  Size = 1.4
FEATURE [PartDesign::Body] Body001  label="Bottom"
  Group = -> [ShapeBinder,ShapeBinder001,Sketch015,Pad008,Sketch016,Pocket005,Sketch019,Pad009,Sketch020,Pocket008,Sketch021,Pad010,Sketch024,Pocket011,Sketch025,Pocket012,Sketch027,Sketch028,Sketch029,Sketch030,DatumPlane,DatumPlane001,DatumPlane002,Sketch032,Sketch033,SubtractiveLoft,SubtractiveLoft001,Sketch034,SubtractiveLoft002,Sketch044,SubtractiveLoft003,Chamfer,Sketch053,Pocket013,Sketch057,Pocket015,+5 more]
  Origin = -> Origin001
  Tip = -> Chamfer005
FEATURE [PartDesign::ShapeBinder] ShapeBinder010
  TraceSupport = false
FEATURE [PartDesign::ShapeBinder] ShapeBinder011
  TraceSupport = false
FEATURE [Sketcher::SketchObject] Sketch079
  ExternalGeometry = -> [ShapeBinder011,ShapeBinder010]
  MapMode = 5
  Support = -> [XY_Plane009]
  sketch-geometry (7):
    g0: LineSegment StartX=40 StartY=105.4 StartZ=0 EndX=82 EndY=105.4 EndZ=0
    g1: LineSegment StartX=88 StartY=99.4 StartZ=0 EndX=88 EndY=73.4 EndZ=0
    g2: LineSegment StartX=80 StartY=81.4 StartZ=0 EndX=34 EndY=81.4 EndZ=0
    g3: LineSegment StartX=34 StartY=81.4 StartZ=0 EndX=34 EndY=99.4 EndZ=0
    g4: ArcOfCircle CenterX=40 CenterY=99.4 CenterZ=0 NormalX=0 NormalY=0 NormalZ=1 AngleXU=0 Radius=6 StartAngle=1.5708 EndAngle=3.14159
    g5: ArcOfCircle CenterX=82 CenterY=99.4 CenterZ=0 NormalX=0 NormalY=0 NormalZ=1 AngleXU=0 Radius=6 StartAngle=-9e-16 EndAngle=1.5708
    g6: ArcOfCircle CenterX=80 CenterY=73.4 CenterZ=0 NormalX=0 NormalY=0 NormalZ=1 AngleXU=0 Radius=8 StartAngle=0 EndAngle=1.5708
  constraints (20):
    c: Horizontal(g0)
    c: Horizontal(g2)
    c: Vertical(g1)
    c: Vertical(g3)
    c: Tangent(g0,g4) = 1.5708
    c: Tangent(g3,g4) = 1.5708
    c: Tangent(g0,g5) = 1.5708
    c: Tangent(g1,g5) = 1.5708
    c: Coincident(g2,g3)
    c: Horizontal(g4,g5)
    c: DistanceY(g-3,g2) = 3
    c: DistanceX(g5,g1) = 6
    c: Radius(g6) = 8
    c: Coincident(g6,g1)
    c: Coincident(g2,g6)
    c: Vertical(g6,g2)
    c: DistanceX(g0,g0) = 42
    c: DistanceY(g3,g3) = 18
    c: DistanceX(g-4,g1) = 3
    c: Horizontal(g1,g6)
FEATURE [PartDesign::Pad] Pad018
  Length = 14
  Length2 = 100
  Profile = -> Sketch079
  Type = 0
FEATURE [Sketcher::SketchObject] Sketch076
  ExternalGeometry = -> [Pad018]
  MapMode = 5
  Placement = pos=(0,0,2) rot=(0,0,1;0rad)
  sketch-geometry (6):
    g0: LineSegment StartX=40 StartY=103.4 StartZ=0 EndX=82 EndY=103.4 EndZ=0
    g1: LineSegment StartX=86 StartY=99.4 StartZ=0 EndX=86 EndY=83.4 EndZ=0
    g2: LineSegment StartX=86 StartY=83.4 StartZ=0 EndX=36 EndY=83.4 EndZ=0
    g3: LineSegment StartX=36 StartY=83.4 StartZ=0 EndX=36 EndY=99.4 EndZ=0
    g4: ArcOfCircle CenterX=40 CenterY=99.4 CenterZ=0 NormalX=0 NormalY=0 NormalZ=1 AngleXU=0 Radius=4 StartAngle=1.5708 EndAngle=3.14159
    g5: ArcOfCircle CenterX=82 CenterY=99.4 CenterZ=0 NormalX=0 NormalY=0 NormalZ=1 AngleXU=0 Radius=4 StartAngle=0 EndAngle=1.5708
  constraints (20):
    c: Coincident(g0,g5)
    c: Coincident(g2,g3)
    c: Coincident(g3,g4)
    c: Coincident(g1,g2)
    c: Coincident(g1,g5)
    c: Coincident(g0,g4)
    c: Horizontal(g0)
    c: Vertical(g1)
    c: Vertical(g3)
    c: Horizontal(g2)
    c: Horizontal(g4,g5)
    c: Horizontal(g3,g4)
    c: Horizontal(g5,g1)
    c: Vertical(g5,g0)
    c: Vertical(g0,g4)
    c: DistanceY(g5,g0) = 4
    c: DistanceX(g-3,g2) = 2
    c: DistanceY(g-3,g2) = 2
    c: DistanceX(g2,g2) = 50
    c: DistanceY(g1,g1) = 16
FEATURE [PartDesign::Pocket] Pocket026
  BaseFeature = -> Pad018
  Length = 12
  Length2 = 100
  Profile = -> Sketch076
  Reversed = true
  Type = 0
FEATURE [PartDesign::Fillet] Fillet004
  Base = -> Pocket026 [Edge2]
  BaseFeature = -> Pocket026
  Radius = 1
FEATURE [PartDesign::ShapeBinder] ShapeBinder012
  TraceSupport = false
FEATURE [PartDesign::ShapeBinder] ShapeBinder013
  TraceSupport = false
FEATURE [PartDesign::Plane] DatumPlane011
  Length = 119.269
  MapMode = 2
  Placement = pos=(0,0,18) rot=(0,0,1;0rad)
  ResizeMode = 0
  Width = 136.669
FEATURE [Sketcher::SketchObject] Sketch085
  ExternalGeometry = -> [ShapeBinder013,ShapeBinder012]
  MapMode = 5
  Placement = pos=(0,0,18) rot=(0,0,1;0rad)
  Support = -> [DatumPlane011]
  sketch-geometry (7):
    g0: LineSegment StartX=40 StartY=105.4 StartZ=0 EndX=82 EndY=105.4 EndZ=0
    g1: LineSegment StartX=88 StartY=99.4 StartZ=0 EndX=88 EndY=73.4 EndZ=0
    g2: LineSegment StartX=80 StartY=81.4 StartZ=0 EndX=34 EndY=81.4 EndZ=0
    g3: LineSegment StartX=34 StartY=81.4 StartZ=0 EndX=34 EndY=99.4 EndZ=0
    g4: ArcOfCircle CenterX=82 CenterY=99.4 CenterZ=0 NormalX=0 NormalY=0 NormalZ=1 AngleXU=0 Radius=6 StartAngle=1e-15 EndAngle=1.5708
    g5: ArcOfCircle CenterX=40 CenterY=99.4 CenterZ=0 NormalX=0 NormalY=0 NormalZ=1 AngleXU=0 Radius=6 StartAngle=1.5708 EndAngle=3.14159
    g6: ArcOfCircle CenterX=80 CenterY=73.4 CenterZ=0 NormalX=0 NormalY=0 NormalZ=1 AngleXU=0 Radius=8 StartAngle=0 EndAngle=1.5708
  constraints (20):
    c: Coincident(g2,g3)
    c: Horizontal(g0)
    c: Horizontal(g2)
    c: Vertical(g1)
    c: Vertical(g3)
    c: Tangent(g0,g4) = 1.5708
    c: Tangent(g1,g4) = 1.5708
    c: Tangent(g0,g5) = 1.5708
    c: Tangent(g3,g5) = 1.5708
    c: DistanceY(g-3,g3) = 3
    c: DistanceY(g3,g3) = 18
    c: DistanceX(g0,g0) = 42
    c: DistanceY(g4,g0) = 6
    c: Horizontal(g5,g4)
    c: Radius(g6) = 8
    c: Coincident(g6,g1)
    c: Coincident(g6,g2)
    c: DistanceX(g-4,g1) = 3
    c: Vertical(g6,g2)
    c: Horizontal(g6,g1)
FEATURE [PartDesign::Pad] Pad019
  Length = 10
  Length2 = 100
  Placement = pos=(0,0,18) rot=(0,0,1;0rad)
  Profile = -> Sketch085
  Reversed = true
  Type = 0
FEATURE [Sketcher::SketchObject] Sketch083
  AttachmentOffset = pos=(0,0,-2) rot=(0,0,1;0rad)
  ExternalGeometry = -> [Pad019]
  MapMode = 5
  Placement = pos=(0,0,16) rot=(0,0,1;0rad)
  Support = -> [Pad019]
  sketch-geometry (6):
    g0: LineSegment StartX=40 StartY=103.4 StartZ=0 EndX=82 EndY=103.4 EndZ=0
    g1: LineSegment StartX=86 StartY=99.4 StartZ=0 EndX=86 EndY=83.4 EndZ=0
    g2: LineSegment StartX=86 StartY=83.4 StartZ=0 EndX=36 EndY=83.4 EndZ=0
    g3: LineSegment StartX=36 StartY=83.4 StartZ=0 EndX=36 EndY=99.4 EndZ=0
    g4: ArcOfCircle CenterX=40 CenterY=99.4 CenterZ=0 NormalX=0 NormalY=0 NormalZ=1 AngleXU=0 Radius=4 StartAngle=1.5708 EndAngle=3.14159
    g5: ArcOfCircle CenterX=82 CenterY=99.4 CenterZ=0 NormalX=0 NormalY=0 NormalZ=1 AngleXU=0 Radius=4 StartAngle=-2.7e-15 EndAngle=1.5708
  constraints (16):
    c: Coincident(g1,g2)
    c: Coincident(g2,g3)
    c: Horizontal(g0)
    c: Horizontal(g2)
    c: Vertical(g1)
    c: Vertical(g3)
    c: Tangent(g0,g4) = 1.5708
    c: Tangent(g3,g4) = 1.5708
    c: Tangent(g0,g5) = 1.5708
    c: Tangent(g1,g5) = 1.5708
    c: DistanceY(g1,g0) = 4
    c: DistanceX(g2,g2) = 50
    c: DistanceY(g1,g1) = 16
    c: DistanceX(g-3,g2) = 2
    c: DistanceY(g-3,g2) = 2
    c: Horizontal(g5,g4)
FEATURE [PartDesign::Plane] DatumPlane012
  Length = 119.269
  MapMode = 2
  Placement = pos=(0,0,14) rot=(0,0,1;0rad)
  ResizeMode = 0
  Width = 136.669
FEATURE [PartDesign::Pocket] Pocket027
  BaseFeature = -> Pad019
  Length = 8
  Length2 = 100
  Placement = pos=(0,0,18) rot=(0,0,1;0rad)
  Profile = -> Sketch083
  Type = 0
FEATURE [PartDesign::Plane] DatumPlane014
  Length = 107.699
  MapMode = 5
  Placement = pos=(0,105.4,0) rot=(0,0.707107,0.707107;3.14159rad)
  ResizeMode = 0
  Support = -> [Fillet004]
  Width = 33.6995
FEATURE [Sketcher::SketchObject] Sketch087
  ExternalGeometry = -> [Fillet004]
  MapMode = 5
  Placement = pos=(0,105.4,0) rot=(0,0.707107,0.707107;3.14159rad)
  Support = -> [DatumPlane014]
  sketch-geometry (14):
    g0: LineSegment StartX=-88 StartY=14 StartZ=0 EndX=-81.2 EndY=14 EndZ=0
    g1: LineSegment StartX=-81.2 StartY=14 StartZ=0 EndX=-81.2 EndY=12.8 EndZ=0
    g2: LineSegment StartX=-81.2 StartY=8 StartZ=0 EndX=-88 EndY=8 EndZ=0
    g3: LineSegment StartX=-88 StartY=8 StartZ=0 EndX=-88 EndY=14 EndZ=0
    g4: LineSegment StartX=-81.2 StartY=12.8 StartZ=0 EndX=-82.8 EndY=11.2 EndZ=0
    g5: LineSegment StartX=-82.8 StartY=11.2 StartZ=0 EndX=-81.2 EndY=9.6 EndZ=0
    g6: LineSegment StartX=-40.8 StartY=14 StartZ=0 EndX=-34 EndY=14 EndZ=0
    g7: LineSegment StartX=-34 StartY=14 StartZ=0 EndX=-34 EndY=8 EndZ=0
    g8: LineSegment StartX=-34 StartY=8 StartZ=0 EndX=-40.8 EndY=8 EndZ=0
    g9: LineSegment StartX=-40.8 StartY=12.8 StartZ=0 EndX=-40.8 EndY=14 EndZ=0
    g10: LineSegment StartX=-40.8 StartY=12.8 StartZ=0 EndX=-39.2 EndY=11.2 EndZ=0
    g11: LineSegment StartX=-39.2 StartY=11.2 StartZ=0 EndX=-40.8 EndY=9.6 EndZ=0
    g12: LineSegment StartX=-81.2 StartY=9.6 StartZ=0 EndX=-81.2 EndY=8 EndZ=0
    g13: LineSegment StartX=-40.8 StartY=9.6 StartZ=0 EndX=-40.8 EndY=8 EndZ=0
  constraints (40):
    c: Coincident(g0,g1)
    c: Coincident(g2,g3)
    c: Coincident(g3,g0)
    c: Horizontal(g0)
    c: Horizontal(g2)
    c: Vertical(g1)
    c: Vertical(g3)
    c: Coincident(g1,g4)
    c: Coincident(g4,g5)
    c: Coincident(g6,g7)
    c: Coincident(g7,g8)
    c: Coincident(g9,g6)
    c: Horizontal(g6)
    c: Horizontal(g8)
    c: Vertical(g7)
    c: Vertical(g9)
    c: Coincident(g9,g10)
    c: Coincident(g10,g11)
    c: Coincident(g0,g-4)
    c: DistanceX(g-3,g0) = 0.8
    c: DistanceX(g6,g-3) = 0.8
    c: Coincident(g6,g-5)
    c: Horizontal(g1,g9)
    c: Horizontal(g4,g10)
    c: Horizontal(g8,g2)
    c: DistanceY(g4,g1) = 1.6
    c: DistanceX(g4,g2) = 1.6
    c: DistanceX(g8,g10) = 1.6
    c: DistanceY(g1,g1) = 1.2
    c: Vertical(g8,g9)
    c: Vertical(g2,g1)
    c: Horizontal(g11,g5)
    c: DistanceY(g5,g4) = 1.6
    c: Vertical(g5,g1)
    c: Vertical(g11,g9)
    c: Coincident(g12,g5)
    c: Coincident(g12,g2)
    c: Coincident(g13,g11)
    c: Coincident(g13,g8)
    c: DistanceY(g12,g12) = 1.6
FEATURE [PartDesign::Pocket] Pocket029
  BaseFeature = -> Fillet004
  Length = 5
  Length2 = 100
  Profile = -> Sketch087
  Type = 1
FEATURE [PartDesign::Plane] DatumPlane015
  Length = 107.699
  MapMode = 5
  Placement = pos=(0,81.4,0) rot=(1,0,0;1.5708rad)
  ResizeMode = 0
  Support = -> [Pocket029]
  Width = 33.6995
FEATURE [Sketcher::SketchObject] Sketch088
  MapMode = 5
  Placement = pos=(0,81.4,0) rot=(1,0,0;1.5708rad)
  Support = -> [DatumPlane015]
  sketch-geometry (5):
    g0: Circle CenterX=63 CenterY=6 CenterZ=0 NormalX=0 NormalY=0 NormalZ=1 AngleXU=0 Radius=1.8
    g1: LineSegment StartX=70 StartY=9 StartZ=0 EndX=79 EndY=9 EndZ=0
    g2: LineSegment StartX=79 StartY=9 StartZ=0 EndX=79 EndY=5 EndZ=0
    g3: LineSegment StartX=79 StartY=5 StartZ=0 EndX=70 EndY=5 EndZ=0
    g4: LineSegment StartX=70 StartY=5 StartZ=0 EndX=70 EndY=9 EndZ=0
  constraints (15):
    c: Coincident(g1,g2)
    c: Coincident(g2,g3)
    c: Coincident(g3,g4)
    c: Coincident(g4,g1)
    c: Horizontal(g1)
    c: Horizontal(g3)
    c: Vertical(g2)
    c: Vertical(g4)
    c: DistanceX(g-1,g0) = 63
    c: Radius(g0) = 1.8
    c: DistanceY(g-1,g0) = 6
    c: DistanceX(g-1,g3) = 70
    c: DistanceY(g-1,g3) = 5
    c: DistanceX(g1,g1) = 9
    c: DistanceY(g2,g2) = 4
FEATURE [PartDesign::Fillet] Fillet005
  Base = -> Pocket027 [Edge26]
  BaseFeature = -> Pocket027
  Placement = pos=(0,0,18) rot=(0,0,1;0rad)
  Radius = 1
FEATURE [PartDesign::Plane] DatumPlane013
  Length = 108.477
  MapMode = 5
  Placement = pos=(0,105.4,18) rot=(0,0.707107,0.707107;3.14159rad)
  ResizeMode = 0
  Support = -> [Fillet005]
  Width = 38.4766
FEATURE [Sketcher::SketchObject] Sketch086
  ExternalGeometry = -> [Fillet005]
  MapMode = 5
  Placement = pos=(0,105.4,18) rot=(0,0.707107,0.707107;3.14159rad)
  Support = -> [DatumPlane013]
  sketch-geometry (10):
    g0: LineSegment StartX=-81.4 StartY=-3.8 StartZ=0 EndX=-40.6 EndY=-3.8 EndZ=0
    g1: LineSegment StartX=-40.6 StartY=-3.8 StartZ=0 EndX=-40.6 EndY=-5.2 EndZ=0
    g2: LineSegment StartX=-40.6 StartY=-10 StartZ=0 EndX=-81.4 EndY=-10 EndZ=0
    g3: LineSegment StartX=-81.4 StartY=-5.2 StartZ=0 EndX=-81.4 EndY=-3.8 EndZ=0
    g4: LineSegment StartX=-81.4 StartY=-5.2 StartZ=0 EndX=-83 EndY=-6.8 EndZ=0
    g5: LineSegment StartX=-83 StartY=-6.8 StartZ=0 EndX=-81.4 EndY=-8.4 EndZ=0
    g6: LineSegment StartX=-40.6 StartY=-5.2 StartZ=0 EndX=-39 EndY=-6.8 EndZ=0
    g7: LineSegment StartX=-39 StartY=-6.8 StartZ=0 EndX=-40.6 EndY=-8.4 EndZ=0
    g8: LineSegment StartX=-81.4 StartY=-8.4 StartZ=0 EndX=-81.4 EndY=-10 EndZ=0
    g9: LineSegment StartX=-40.6 StartY=-10 StartZ=0 EndX=-40.6 EndY=-8.4 EndZ=0
  constraints (30):
    c: Coincident(g0,g1)
    c: Coincident(g3,g0)
    c: Horizontal(g0)
    c: Horizontal(g2)
    c: Vertical(g1)
    c: Vertical(g3)
    c: Coincident(g4,g5)
    c: Coincident(g6,g7)
    c: Coincident(g4,g3)
    c: Coincident(g1,g6)
    c: Vertical(g3,g2)
    c: Vertical(g1,g2)
    c: Horizontal(g3,g1)
    c: Horizontal(g4,g6)
    c: DistanceY(g1,g1) = 1.4
    c: DistanceY(g6,g1) = 1.6
    c: DistanceX(g2,g6) = 1.6
    c: DistanceX(g4,g2) = 1.6
    c: DistanceX(g-3,g0) = 0.6
    c: DistanceX(g0,g-3) = 0.6
    c: Coincident(g8,g5)
    c: Coincident(g8,g2)
    c: Vertical(g8)
    c: Coincident(g9,g2)
    c: Coincident(g9,g7)
    c: Vertical(g9)
    c: Horizontal(g5,g7)
    c: DistanceY(g7,g6) = 1.6
    c: PointOnObject(g2,g-3)
    c: DistanceY(g9,g9) = 1.6
FEATURE [PartDesign::Pocket] Pocket028
  BaseFeature = -> Fillet005
  Length = 5
  Length2 = 100
  Placement = pos=(0,0,18) rot=(0,0,1;0rad)
  Profile = -> Sketch086
  Type = 1
FEATURE [PartDesign::Pocket] Pocket030
  BaseFeature = -> Pocket029
  Length = 2
  Length2 = 100
  Profile = -> Sketch088
  Type = 0
FEATURE [PartDesign::Plane] DatumPlane016
  Length = 119.269
  MapMode = 5
  Placement = pos=(0,0,8) rot=(1,0,0;3.14159rad)
  ResizeMode = 0
  Support = -> [Pocket028]
  Width = 136.669
FEATURE [Sketcher::SketchObject] Sketch089
  ExternalGeometry = -> [Pocket028]
  MapMode = 5
  Placement = pos=(0,0,8) rot=(1,0,0;3.14159rad)
  Support = -> [DatumPlane016]
  sketch-geometry (8):
    g0: LineSegment StartX=34 StartY=-86.4 StartZ=0 EndX=36 EndY=-86.4 EndZ=0
    g1: LineSegment StartX=36 StartY=-86.4 StartZ=0 EndX=36 EndY=-92.8 EndZ=0
    g2: LineSegment StartX=36 StartY=-92.8 StartZ=0 EndX=34 EndY=-92.8 EndZ=0
    g3: LineSegment StartX=34 StartY=-92.8 StartZ=0 EndX=34 EndY=-86.4 EndZ=0
    g4: LineSegment StartX=86 StartY=-86.4 StartZ=0 EndX=88 EndY=-86.4 EndZ=0
    g5: LineSegment StartX=88 StartY=-86.4 StartZ=0 EndX=88 EndY=-92.8 EndZ=0
    g6: LineSegment StartX=88 StartY=-92.8 StartZ=0 EndX=86 EndY=-92.8 EndZ=0
    g7: LineSegment StartX=86 StartY=-92.8 StartZ=0 EndX=86 EndY=-86.4 EndZ=0
  constraints (24):
    c: Coincident(g0,g1)
    c: Coincident(g1,g2)
    c: Coincident(g2,g3)
    c: Coincident(g3,g0)
    c: Horizontal(g0)
    c: Horizontal(g2)
    c: Vertical(g1)
    c: Vertical(g3)
    c: Coincident(g4,g5)
    c: Coincident(g5,g6)
    c: Coincident(g6,g7)
    c: Coincident(g7,g4)
    c: Horizontal(g4)
    c: Horizontal(g6)
    c: Vertical(g5)
    c: Vertical(g7)
    c: Equal(g0,g4)
    c: Equal(g3,g7)
    c: PointOnObject(g0,g-3)
    c: PointOnObject(g4,g-4)
    c: DistanceX(g4,g4) = 2
    c: DistanceY(g5,g5) = 6.4
    c: DistanceY(g0,g-3) = 3
    c: Horizontal(g0,g4)
FEATURE [PartDesign::Pocket] Pocket031
  BaseFeature = -> Pocket028
  Length = 3
  Length2 = 100
  Placement = pos=(0,0,18) rot=(0,0,1;0rad)
  Profile = -> Sketch089
  Type = 0
FEATURE [PartDesign::Body] Body009  label="Antenna-Horz-Cover"
  Group = -> [ShapeBinder013,ShapeBinder012,DatumPlane011,Sketch085,Pad019,DatumPlane012,Sketch083,Pocket027,Fillet005,DatumPlane013,Sketch086,Pocket028,DatumPlane016,Sketch089,Pocket031]
  Origin = -> Origin009
  Tip = -> Pocket031
FEATURE [PartDesign::Plane] DatumPlane017
  Length = 119.269
  MapMode = 5
  Placement = pos=(0,1.8e-15,8) rot=(0,0,1;0rad)
  ResizeMode = 0
  Support = -> [Pocket030]
  Width = 136.669
FEATURE [Sketcher::SketchObject] Sketch090
  ExternalGeometry = -> [Pocket030]
  MapMode = 5
  Placement = pos=(0,1.8e-15,8) rot=(0,0,1;0rad)
  Support = -> [DatumPlane017]
  sketch-geometry (8):
    g0: LineSegment StartX=34 StartY=92.6 StartZ=0 EndX=36 EndY=92.6 EndZ=0
    g1: LineSegment StartX=36 StartY=92.6 StartZ=0 EndX=36 EndY=86.6 EndZ=0
    g2: LineSegment StartX=36 StartY=86.6 StartZ=0 EndX=34 EndY=86.6 EndZ=0
    g3: LineSegment StartX=34 StartY=86.6 StartZ=0 EndX=34 EndY=92.6 EndZ=0
    g4: LineSegment StartX=86 StartY=92.6 StartZ=0 EndX=88 EndY=92.6 EndZ=0
    g5: LineSegment StartX=88 StartY=92.6 StartZ=0 EndX=88 EndY=86.6 EndZ=0
    g6: LineSegment StartX=88 StartY=86.6 StartZ=0 EndX=86 EndY=86.6 EndZ=0
    g7: LineSegment StartX=86 StartY=86.6 StartZ=0 EndX=86 EndY=92.6 EndZ=0
  constraints (24):
    c: Coincident(g0,g1)
    c: Coincident(g1,g2)
    c: Coincident(g2,g3)
    c: Coincident(g3,g0)
    c: Horizontal(g0)
    c: Horizontal(g2)
    c: Vertical(g1)
    c: Vertical(g3)
    c: Coincident(g4,g5)
    c: Coincident(g5,g6)
    c: Coincident(g6,g7)
    c: Coincident(g7,g4)
    c: Horizontal(g4)
    c: Horizontal(g6)
    c: Vertical(g5)
    c: Vertical(g7)
    c: Equal(g1,g7)
    c: Equal(g0,g4)
    c: DistanceX(g4,g4) = 2
    c: PointOnObject(g4,g-4)
    c: PointOnObject(g0,g-3)
    c: Horizontal(g1,g6)
    c: DistanceY(g-3,g1) = 3.2
    c: DistanceY(g3,g3) = 6
FEATURE [PartDesign::Pad] Pad020
  BaseFeature = -> Pocket030
  Length = 2.8
  Length2 = 100
  Profile = -> Sketch090
  Type = 0
FEATURE [PartDesign::Body] Body008  label="Antenna-Horz-Bottom"
  Group = -> [ShapeBinder011,ShapeBinder010,Sketch079,Pad018,Sketch076,Pocket026,Fillet004,DatumPlane014,Sketch087,Pocket029,DatumPlane015,Sketch088,Pocket030,DatumPlane017,Sketch090,Pad020]
  Origin = -> Origin008
  Tip = -> Pad020
FEATURE [Mesh::Feature] Mesh  label="Antenna-Horz-Bottom (Meshed)"
FEATURE [Mesh::Feature] Mesh001  label="Antenna-Horz-Cover (Meshed)"
